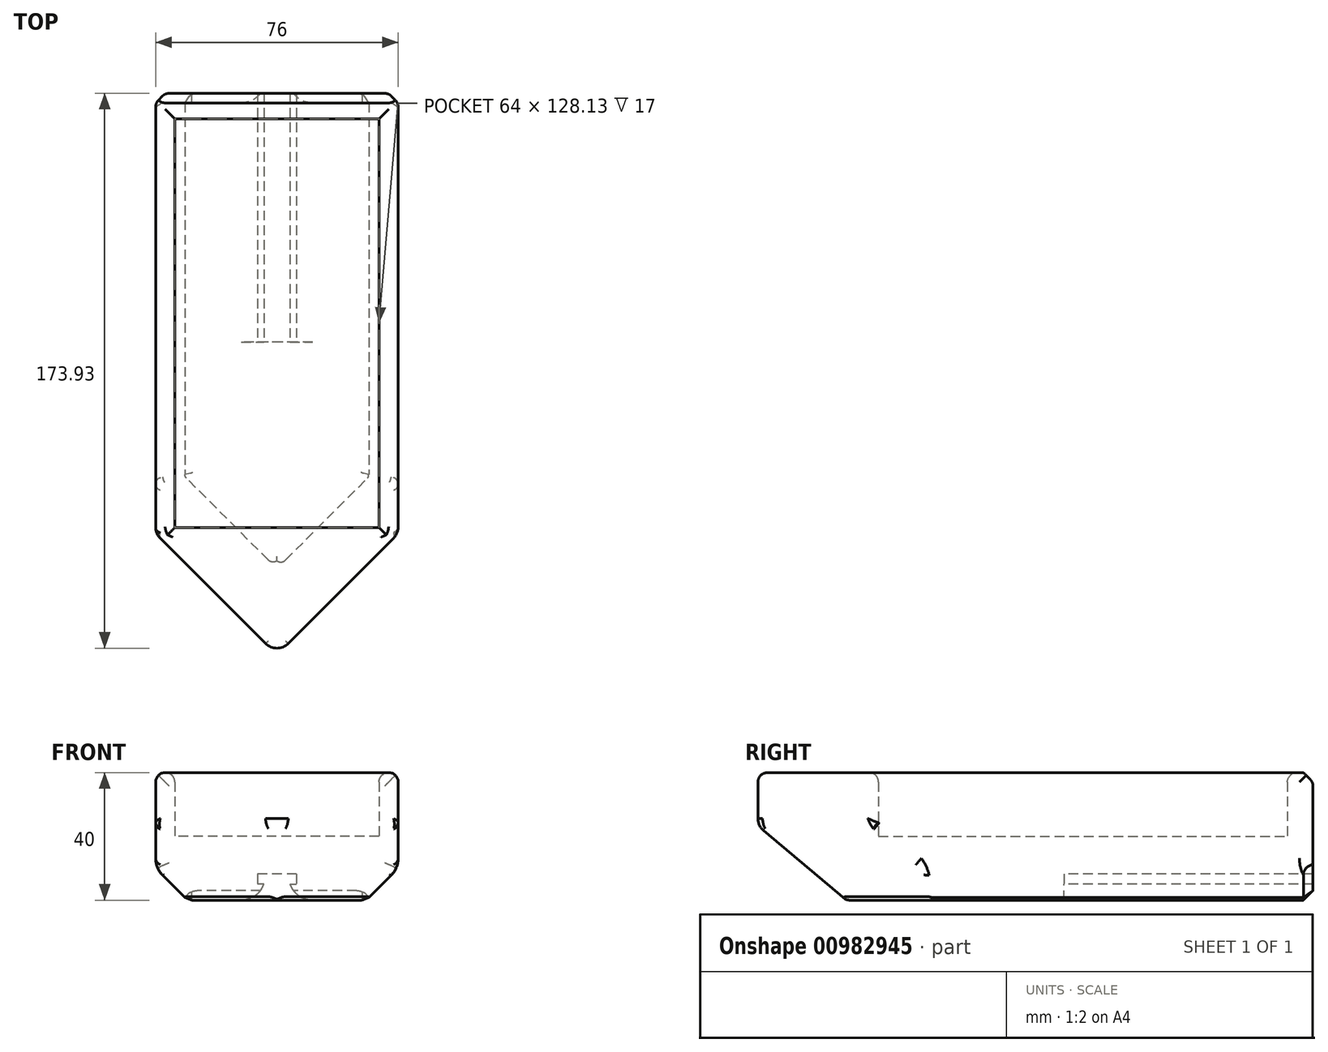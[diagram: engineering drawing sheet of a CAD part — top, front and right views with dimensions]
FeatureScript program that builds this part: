
annotation { "Feature Type Name" : "Feature", "Feature Type Description" : "" }
export const myFeature = defineFeature(function(context is Context, id is Id, definition is map)
    precondition{}
    {
        {
            var Q0;
            Q0=qCreatedBy(makeId("Front.planeOp"),FACE);
            var sketch = newSketch(context, id + "F0", { "sketchPlane" : qUnion([Q0])});
            skLineSegment(sketch, "E0", {"start": v(-6.12, 0) * mm, "end": v(-4.1, 0) * mm});
            skLineSegment(sketch, "E1", {"start": v(-4.1, 0) * mm, "end": v(-4.1, -5) * mm});
            skLineSegment(sketch, "E2", {"start": v(-4.1, -5) * mm, "end": v(-11.1, -5) * mm});
            skLineSegment(sketch, "E3", {"start": v(-11.1, -5) * mm, "end": v(-21.1, -5) * mm});
            skLineSegment(sketch, "E4", {"start": v(-6.12, 0) * mm, "end": v(-6.12, 3.2) * mm});
            skLineSegment(sketch, "E5", {"start": v(-6.12, 3.2) * mm, "end": v(0, 3.2) * mm});
            skLineSegment(sketch, "E6", {"start": v(-21.1, -5) * mm, "end": v(-38, -5) * mm});
            skLineSegment(sketch, "E7", {"start": v(-38, -5) * mm, "end": v(-38, 35) * mm});
            skLineSegment(sketch, "E8", {"start": v(-38, 35) * mm, "end": v(-32, 35) * mm});
            skLineSegment(sketch, "E9", {"start": v(-32, 35) * mm, "end": v(-32, 15) * mm});
            skLineSegment(sketch, "E10", {"start": v(-32, 15) * mm, "end": v(0, 15) * mm});
            skLineSegment(sketch, "E11", {"start": v(-32, 35) * mm, "end": v(0, 35) * mm});
            skLineSegment(sketch, "E12", {"start": v(0, 3.2) * mm, "end": v(0, 35) * mm, "construction": true});
            skLineSegment(sketch, "E13.MirrorCS", {"start": v(6.12, 0) * mm, "end": v(4.1, 0) * mm});
            skLineSegment(sketch, "E14.MirrorCS", {"start": v(6.12, 3.2) * mm, "end": v(0, 3.2) * mm});
            skLineSegment(sketch, "E15.MirrorCS", {"start": v(32, 35) * mm, "end": v(0, 35) * mm});
            skLineSegment(sketch, "E16.MirrorCS", {"start": v(6.12, 0) * mm, "end": v(6.12, 3.2) * mm});
            skLineSegment(sketch, "E17.MirrorCS", {"start": v(32, 15) * mm, "end": v(0, 15) * mm});
            skLineSegment(sketch, "E18.MirrorCS", {"start": v(11.1, -5) * mm, "end": v(21.1, -5) * mm});
            skLineSegment(sketch, "E19.MirrorCS", {"start": v(32, 35) * mm, "end": v(32, 15) * mm});
            skLineSegment(sketch, "E20.MirrorCS", {"start": v(4.1, -5) * mm, "end": v(11.1, -5) * mm});
            skLineSegment(sketch, "E21.MirrorCS", {"start": v(38, 35) * mm, "end": v(32, 35) * mm});
            skLineSegment(sketch, "E22.MirrorCS", {"start": v(4.1, 0) * mm, "end": v(4.1, -5) * mm});
            skLineSegment(sketch, "E23.MirrorCS", {"start": v(38, -5) * mm, "end": v(38, 35) * mm});
            skLineSegment(sketch, "E24.MirrorCS", {"start": v(21.1, -5) * mm, "end": v(38, -5) * mm});
            skLineSegment(sketch, "E25", {"start": v(21.1, -5) * mm, "end": v(-21.1, -5) * mm});
            skLineSegment(sketch, "E26", {"start": v(4.1, -5) * mm, "end": v(-4.1, -5) * mm});
            skSolve(sketch);
        }
        {
            var Q0;
            Q0=makeQuery(id+"F0.imprint","IMPRINT",FACE,{"disambiguationData":[TD([[makeQuery(id+"F0.imprint","IMPRINT",EDGE,{"derivedFrom":sQuery(id+"F0.wireOp",EDGE,"E0")}),-1.0]])]});
            var Q1;
            Q1=makeQuery(id+"F0.imprint","IMPRINT",FACE,{"disambiguationData":[TD([[makeQuery(id+"F0.imprint","IMPRINT",EDGE,{"derivedFrom":sQuery(id+"F0.wireOp",EDGE,"E9")}),1.0]])]});
            var Q2;
            Q2=makeQuery(id+"F0.imprint","IMPRINT",FACE,{"disambiguationData":[TD([[makeQuery(id+"F0.imprint","IMPRINT",EDGE,{"derivedFrom":sQuery(id+"F0.wireOp",EDGE,"E6")}),-1.0]])]});
            extrude(context, id + "F1", {"entities" : qUnion([Q0, Q1, Q2]), "oppositeDirection" : true, "depth" : 8 * mm, "offsetDistance" : 25 * mm});
        }
        {
            var Q0;
            Q0=makeQuery(id+"F0.imprint","IMPRINT",FACE,{"disambiguationData":[TD([[makeQuery(id+"F0.imprint","IMPRINT",EDGE,{"derivedFrom":sQuery(id+"F0.wireOp",EDGE,"E6")}),-1.0]])]});
            extrude(context, id + "F2", {"entities" : qUnion([Q0]), "operationType" : NewBodyOperationType.ADD, "depth" : 130 * mm, "offsetDistance" : 25 * mm});
        }
        {
            var Q0;
            Q0=makeQuery(id+"F0.imprint","IMPRINT",FACE,{"disambiguationData":[TD([[makeQuery(id+"F0.imprint","IMPRINT",EDGE,{"derivedFrom":sQuery(id+"F0.wireOp",EDGE,"E6")}),-1.0]])]});
            var Q1;
            Q1=makeQuery(id+"F0.imprint","IMPRINT",FACE,{"disambiguationData":[TD([[makeQuery(id+"F0.imprint","IMPRINT",EDGE,{"derivedFrom":sQuery(id+"F0.wireOp",EDGE,"E9")}),1.0]])]});
            extrude(context, id + "F3", {"entities" : qUnion([Q0, Q1]), "operationType" : NewBodyOperationType.ADD, "depth" : 170 * mm, "offsetDistance" : 25 * mm, "hasSecondDirection" : true, "secondDirectionOppositeDirection" : false, "secondDirectionDepth" : 128.13 * mm});
        }
        {
            var Q0;
            Q0=makeQuery(id+"F0.imprint","IMPRINT",FACE,{"disambiguationData":[TD([[makeQuery(id+"F0.imprint","IMPRINT",EDGE,{"derivedFrom":sQuery(id+"F0.wireOp",EDGE,"E0")}),-1.0]])]});
            extrude(context, id + "F4", {"entities" : qUnion([Q0]), "operationType" : NewBodyOperationType.ADD, "depth" : 90 * mm, "offsetDistance" : 25 * mm});
        }
        {
            var Q0;
            Q0=makeQuery(id+"F0.imprint","IMPRINT",FACE,{"disambiguationData":[TD([[makeQuery(id+"F0.imprint","IMPRINT",EDGE,{"derivedFrom":sQuery(id+"F0.wireOp",EDGE,"E0")}),-1.0]])]});
            var Q1;
            Q1=makeQuery(id+"F0.imprint","IMPRINT",FACE,{"disambiguationData":[TD([[makeQuery(id+"F0.imprint","IMPRINT",EDGE,{"derivedFrom":sQuery(id+"F0.wireOp",EDGE,"E0")}),1.0]])]});
            extrude(context, id + "F5", {"entities" : qUnion([Q0, Q1]), "operationType" : NewBodyOperationType.ADD, "depth" : 170 * mm, "offsetDistance" : 25 * mm, "hasSecondDirection" : true, "secondDirectionOppositeDirection" : false, "secondDirectionDepth" : 70 * mm});
        }
        {
            var Q0;
            Q0=makeQuery(id+"F5.opExtrude","CAP_EDGE",EDGE,{"disambiguationData":[OSD([sQuery(id+"F0.wireOp",EDGE,"E2"),sQuery(id+"F0.wireOp",EDGE,"E20.MirrorCS"),sQuery(id+"F0.wireOp",EDGE,"E26")])],"isStart":false});
            var Q1;
            {var subQ0=sQuery(id+"F0.wireOp",EDGE,"E25");var subQ1=sQuery(id+"F0.wireOp",EDGE,"E3");var subQ2=sQuery(id+"F0.wireOp",EDGE,"E6");Q1=makeQuery(id+"F12.opFillet","BLEND_EDGE",EDGE,{"blendedFrom":[makeQuery(id+"F5.boolean.opBoolean","MERGE",EDGE,{"derivedFrom":[makeQuery(id+"F4.boolean.opBoolean","MERGE",EDGE,{"derivedFrom":[makeQuery(id+"F1.opExtrude","SWEPT_EDGE",EDGE,{"disambiguationData":[OSD([subQ1,subQ2,subQ0])]}),makeQuery(id+"F4.opExtrude","SWEPT_EDGE",EDGE,{"disambiguationData":[OSD([subQ1,subQ2,subQ0])]})]}),makeQuery(id+"F5.opExtrude","SWEPT_EDGE",EDGE,{"disambiguationData":[OSD([subQ1,subQ2,subQ0])]})]}),makeQuery(id+"F5.opExtrude","CAP_FACE",FACE,{"disambiguationData":[OSD([sQuery(id+"F0.wireOp",EDGE,"E2"),subQ1,sQuery(id+"F0.wireOp",EDGE,"E18.MirrorCS"),sQuery(id+"F0.wireOp",EDGE,"E20.MirrorCS"),subQ0,sQuery(id+"F0.wireOp",EDGE,"E26")])],"isStart":false})],"blendedInto":[makeQuery(id+"F5.opExtrude","CAP_FACE",FACE,{"disambiguationData":[OSD([sQuery(id+"F0.wireOp",EDGE,"E2"),subQ1,sQuery(id+"F0.wireOp",EDGE,"E18.MirrorCS"),sQuery(id+"F0.wireOp",EDGE,"E20.MirrorCS"),subQ0,sQuery(id+"F0.wireOp",EDGE,"E26")])],"isStart":false})]});}
            chamfer(context, id + "F6", {"entities" : qUnion([Q0, Q1]), "width" : 15 * mm, "tangentPropagation" : true});
        }
        {
            var Q0;
            Q0=makeQuery(id+"F3.opExtrude","CAP_EDGE",EDGE,{"disambiguationData":[OSD([sQuery(id+"F0.wireOp",EDGE,"E23.MirrorCS")])],"isStart":false});
            var Q1;
            Q1=makeQuery(id+"F3.opExtrude","CAP_EDGE",EDGE,{"disambiguationData":[OSD([sQuery(id+"F0.wireOp",EDGE,"E7")])],"isStart":false});
            chamfer(context, id + "F7", {"entities" : qUnion([Q0, Q1]), "chamferType" : ChamferType.OFFSET_ANGLE, "width" : 40 * mm, "oppositeDirection" : false, "angle" : 45 * degree, "tangentPropagation" : true});
        }
        {
            var Q0;
            {var subQ0=sQuery(id+"F0.wireOp",EDGE,"E24.MirrorCS");var subQ1=sQuery(id+"F0.wireOp",EDGE,"E6");Q0=makeQuery(id+"F7.opChamfer","BLEND_EDGE",EDGE,{"blendedFrom":[makeQuery(id+"F3.opExtrude","CAP_EDGE",EDGE,{"disambiguationData":[OSD([sQuery(id+"F0.wireOp",EDGE,"E23.MirrorCS")])],"isStart":false}),makeQuery(id+"F3.boolean.opBoolean","MERGE",FACE,{"derivedFrom":[makeQuery(id+"F2.boolean.opBoolean","MERGE",FACE,{"derivedFrom":[makeQuery(id+"F1.opExtrude","SWEPT_FACE",FACE,{"disambiguationData":[OSD([subQ1])]}),makeQuery(id+"F2.opExtrude","SWEPT_FACE",FACE,{"disambiguationData":[OSD([subQ1])]})]}),makeQuery(id+"F2.boolean.opBoolean","MERGE",FACE,{"derivedFrom":[makeQuery(id+"F1.opExtrude","SWEPT_FACE",FACE,{"disambiguationData":[OSD([subQ0])]}),makeQuery(id+"F2.opExtrude","SWEPT_FACE",FACE,{"disambiguationData":[OSD([subQ0])]})]}),makeQuery(id+"F3.opExtrude","SWEPT_FACE",FACE,{"disambiguationData":[OSD([subQ1,subQ0,sQuery(id+"F0.wireOp",EDGE,"E25")])]})]})],"blendedInto":[makeQuery(id+"F3.boolean.opBoolean","MERGE",FACE,{"derivedFrom":[makeQuery(id+"F2.boolean.opBoolean","MERGE",FACE,{"derivedFrom":[makeQuery(id+"F1.opExtrude","SWEPT_FACE",FACE,{"disambiguationData":[OSD([subQ1])]}),makeQuery(id+"F2.opExtrude","SWEPT_FACE",FACE,{"disambiguationData":[OSD([subQ1])]})]}),makeQuery(id+"F2.boolean.opBoolean","MERGE",FACE,{"derivedFrom":[makeQuery(id+"F1.opExtrude","SWEPT_FACE",FACE,{"disambiguationData":[OSD([subQ0])]}),makeQuery(id+"F2.opExtrude","SWEPT_FACE",FACE,{"disambiguationData":[OSD([subQ0])]})]}),makeQuery(id+"F3.opExtrude","SWEPT_FACE",FACE,{"disambiguationData":[OSD([subQ1,subQ0,sQuery(id+"F0.wireOp",EDGE,"E25")])]})]})]});}
            var Q1;
            {var subQ0=sQuery(id+"F0.wireOp",EDGE,"E24.MirrorCS");var subQ1=sQuery(id+"F0.wireOp",EDGE,"E6");Q1=makeQuery(id+"F7.opChamfer","BLEND_EDGE",EDGE,{"blendedFrom":[makeQuery(id+"F3.opExtrude","CAP_EDGE",EDGE,{"disambiguationData":[OSD([sQuery(id+"F0.wireOp",EDGE,"E7")])],"isStart":false}),makeQuery(id+"F3.boolean.opBoolean","MERGE",FACE,{"derivedFrom":[makeQuery(id+"F2.boolean.opBoolean","MERGE",FACE,{"derivedFrom":[makeQuery(id+"F1.opExtrude","SWEPT_FACE",FACE,{"disambiguationData":[OSD([subQ1])]}),makeQuery(id+"F2.opExtrude","SWEPT_FACE",FACE,{"disambiguationData":[OSD([subQ1])]})]}),makeQuery(id+"F2.boolean.opBoolean","MERGE",FACE,{"derivedFrom":[makeQuery(id+"F1.opExtrude","SWEPT_FACE",FACE,{"disambiguationData":[OSD([subQ0])]}),makeQuery(id+"F2.opExtrude","SWEPT_FACE",FACE,{"disambiguationData":[OSD([subQ0])]})]}),makeQuery(id+"F3.opExtrude","SWEPT_FACE",FACE,{"disambiguationData":[OSD([subQ1,subQ0,sQuery(id+"F0.wireOp",EDGE,"E25")])]})]})],"blendedInto":[makeQuery(id+"F3.boolean.opBoolean","MERGE",FACE,{"derivedFrom":[makeQuery(id+"F2.boolean.opBoolean","MERGE",FACE,{"derivedFrom":[makeQuery(id+"F1.opExtrude","SWEPT_FACE",FACE,{"disambiguationData":[OSD([subQ1])]}),makeQuery(id+"F2.opExtrude","SWEPT_FACE",FACE,{"disambiguationData":[OSD([subQ1])]})]}),makeQuery(id+"F2.boolean.opBoolean","MERGE",FACE,{"derivedFrom":[makeQuery(id+"F1.opExtrude","SWEPT_FACE",FACE,{"disambiguationData":[OSD([subQ0])]}),makeQuery(id+"F2.opExtrude","SWEPT_FACE",FACE,{"disambiguationData":[OSD([subQ0])]})]}),makeQuery(id+"F3.opExtrude","SWEPT_FACE",FACE,{"disambiguationData":[OSD([subQ1,subQ0,sQuery(id+"F0.wireOp",EDGE,"E25")])]})]})]});}
            chamfer(context, id + "F8", {"entities" : qUnion([Q0, Q1]), "chamferType" : ChamferType.OFFSET_ANGLE, "width" : 20 * mm, "oppositeDirection" : false, "angle" : 50 * degree, "tangentPropagation" : true});
        }
        {
            var Q0;
            {var subQ0=sQuery(id+"F0.wireOp",EDGE,"E7");var subQ1=sQuery(id+"F0.wireOp",EDGE,"E6");Q0=makeQuery(id+"F3.boolean.opBoolean","MERGE",EDGE,{"derivedFrom":[makeQuery(id+"F2.boolean.opBoolean","MERGE",EDGE,{"derivedFrom":[makeQuery(id+"F1.opExtrude","SWEPT_EDGE",EDGE,{"disambiguationData":[OSD([subQ1,subQ0])]}),makeQuery(id+"F2.opExtrude","SWEPT_EDGE",EDGE,{"disambiguationData":[OSD([subQ1,subQ0])]})]}),makeQuery(id+"F3.opExtrude","SWEPT_EDGE",EDGE,{"disambiguationData":[OSD([subQ1,subQ0])]})]});}
            var Q1;
            {var subQ0=sQuery(id+"F0.wireOp",EDGE,"E24.MirrorCS");var subQ1=sQuery(id+"F0.wireOp",EDGE,"E23.MirrorCS");Q1=makeQuery(id+"F3.boolean.opBoolean","MERGE",EDGE,{"derivedFrom":[makeQuery(id+"F2.boolean.opBoolean","MERGE",EDGE,{"derivedFrom":[makeQuery(id+"F1.opExtrude","SWEPT_EDGE",EDGE,{"disambiguationData":[OSD([subQ1,subQ0])]}),makeQuery(id+"F2.opExtrude","SWEPT_EDGE",EDGE,{"disambiguationData":[OSD([subQ1,subQ0])]})]}),makeQuery(id+"F3.opExtrude","SWEPT_EDGE",EDGE,{"disambiguationData":[OSD([subQ1,subQ0])]})]});}
            chamfer(context, id + "F9", {"entities" : qUnion([Q0, Q1]), "width" : 10 * mm, "tangentPropagation" : true});
        }
        {
            var Q0;
            Q0=makeQuery(id+"F1.opExtrude","CAP_EDGE",EDGE,{"disambiguationData":[OSD([sQuery(id+"F0.wireOp",EDGE,"E8"),sQuery(id+"F0.wireOp",EDGE,"E11"),sQuery(id+"F0.wireOp",EDGE,"E15.MirrorCS"),sQuery(id+"F0.wireOp",EDGE,"E21.MirrorCS")])],"isStart":false});
            var Q1;
            Q1=makeQuery(id+"F1.opExtrude","CAP_EDGE",EDGE,{"disambiguationData":[OSD([sQuery(id+"F0.wireOp",EDGE,"E23.MirrorCS")])],"isStart":false});
            var Q2;
            {var subQ0=sQuery(id+"F0.wireOp",EDGE,"E24.MirrorCS");var subQ1=sQuery(id+"F0.wireOp",EDGE,"E23.MirrorCS");Q2=makeQuery(id+"F9.opChamfer","BLEND_EDGE",EDGE,{"blendedFrom":[makeQuery(id+"F3.boolean.opBoolean","MERGE",EDGE,{"derivedFrom":[makeQuery(id+"F2.boolean.opBoolean","MERGE",EDGE,{"derivedFrom":[makeQuery(id+"F1.opExtrude","SWEPT_EDGE",EDGE,{"disambiguationData":[OSD([subQ1,subQ0])]}),makeQuery(id+"F2.opExtrude","SWEPT_EDGE",EDGE,{"disambiguationData":[OSD([subQ1,subQ0])]})]}),makeQuery(id+"F3.opExtrude","SWEPT_EDGE",EDGE,{"disambiguationData":[OSD([subQ1,subQ0])]})]}),makeQuery(id+"F1.opExtrude","CAP_FACE",FACE,{"disambiguationData":[OSD([sQuery(id+"F0.wireOp",EDGE,"E0"),sQuery(id+"F0.wireOp",EDGE,"E1"),sQuery(id+"F0.wireOp",EDGE,"E2"),sQuery(id+"F0.wireOp",EDGE,"E3"),sQuery(id+"F0.wireOp",EDGE,"E4"),sQuery(id+"F0.wireOp",EDGE,"E5"),sQuery(id+"F0.wireOp",EDGE,"E6"),sQuery(id+"F0.wireOp",EDGE,"E7"),sQuery(id+"F0.wireOp",EDGE,"E8"),sQuery(id+"F0.wireOp",EDGE,"E11"),sQuery(id+"F0.wireOp",EDGE,"E13.MirrorCS"),sQuery(id+"F0.wireOp",EDGE,"E14.MirrorCS"),sQuery(id+"F0.wireOp",EDGE,"E15.MirrorCS"),sQuery(id+"F0.wireOp",EDGE,"E16.MirrorCS"),sQuery(id+"F0.wireOp",EDGE,"E18.MirrorCS"),sQuery(id+"F0.wireOp",EDGE,"E20.MirrorCS"),sQuery(id+"F0.wireOp",EDGE,"E21.MirrorCS"),sQuery(id+"F0.wireOp",EDGE,"E22.MirrorCS"),subQ1,subQ0])],"isStart":false})],"blendedInto":[makeQuery(id+"F1.opExtrude","CAP_FACE",FACE,{"disambiguationData":[OSD([sQuery(id+"F0.wireOp",EDGE,"E0"),sQuery(id+"F0.wireOp",EDGE,"E1"),sQuery(id+"F0.wireOp",EDGE,"E2"),sQuery(id+"F0.wireOp",EDGE,"E3"),sQuery(id+"F0.wireOp",EDGE,"E4"),sQuery(id+"F0.wireOp",EDGE,"E5"),sQuery(id+"F0.wireOp",EDGE,"E6"),sQuery(id+"F0.wireOp",EDGE,"E7"),sQuery(id+"F0.wireOp",EDGE,"E8"),sQuery(id+"F0.wireOp",EDGE,"E11"),sQuery(id+"F0.wireOp",EDGE,"E13.MirrorCS"),sQuery(id+"F0.wireOp",EDGE,"E14.MirrorCS"),sQuery(id+"F0.wireOp",EDGE,"E15.MirrorCS"),sQuery(id+"F0.wireOp",EDGE,"E16.MirrorCS"),sQuery(id+"F0.wireOp",EDGE,"E18.MirrorCS"),sQuery(id+"F0.wireOp",EDGE,"E20.MirrorCS"),sQuery(id+"F0.wireOp",EDGE,"E21.MirrorCS"),sQuery(id+"F0.wireOp",EDGE,"E22.MirrorCS"),subQ1,subQ0])],"isStart":false})]});}
            var Q3;
            Q3=makeQuery(id+"F1.opExtrude","CAP_EDGE",EDGE,{"disambiguationData":[OSD([sQuery(id+"F0.wireOp",EDGE,"E24.MirrorCS")])],"isStart":false});
            var Q4;
            Q4=makeQuery(id+"F1.opExtrude","CAP_EDGE",EDGE,{"disambiguationData":[OSD([sQuery(id+"F0.wireOp",EDGE,"E18.MirrorCS")])],"isStart":false});
            var Q5;
            Q5=makeQuery(id+"F1.opExtrude","CAP_EDGE",EDGE,{"disambiguationData":[OSD([sQuery(id+"F0.wireOp",EDGE,"E3")])],"isStart":false});
            var Q6;
            Q6=makeQuery(id+"F1.opExtrude","CAP_EDGE",EDGE,{"disambiguationData":[OSD([sQuery(id+"F0.wireOp",EDGE,"E6")])],"isStart":false});
            var Q7;
            {var subQ0=sQuery(id+"F0.wireOp",EDGE,"E7");var subQ1=sQuery(id+"F0.wireOp",EDGE,"E6");Q7=makeQuery(id+"F9.opChamfer","BLEND_EDGE",EDGE,{"blendedFrom":[makeQuery(id+"F3.boolean.opBoolean","MERGE",EDGE,{"derivedFrom":[makeQuery(id+"F2.boolean.opBoolean","MERGE",EDGE,{"derivedFrom":[makeQuery(id+"F1.opExtrude","SWEPT_EDGE",EDGE,{"disambiguationData":[OSD([subQ1,subQ0])]}),makeQuery(id+"F2.opExtrude","SWEPT_EDGE",EDGE,{"disambiguationData":[OSD([subQ1,subQ0])]})]}),makeQuery(id+"F3.opExtrude","SWEPT_EDGE",EDGE,{"disambiguationData":[OSD([subQ1,subQ0])]})]}),makeQuery(id+"F1.opExtrude","CAP_FACE",FACE,{"disambiguationData":[OSD([sQuery(id+"F0.wireOp",EDGE,"E0"),sQuery(id+"F0.wireOp",EDGE,"E1"),sQuery(id+"F0.wireOp",EDGE,"E2"),sQuery(id+"F0.wireOp",EDGE,"E3"),sQuery(id+"F0.wireOp",EDGE,"E4"),sQuery(id+"F0.wireOp",EDGE,"E5"),subQ1,subQ0,sQuery(id+"F0.wireOp",EDGE,"E8"),sQuery(id+"F0.wireOp",EDGE,"E11"),sQuery(id+"F0.wireOp",EDGE,"E13.MirrorCS"),sQuery(id+"F0.wireOp",EDGE,"E14.MirrorCS"),sQuery(id+"F0.wireOp",EDGE,"E15.MirrorCS"),sQuery(id+"F0.wireOp",EDGE,"E16.MirrorCS"),sQuery(id+"F0.wireOp",EDGE,"E18.MirrorCS"),sQuery(id+"F0.wireOp",EDGE,"E20.MirrorCS"),sQuery(id+"F0.wireOp",EDGE,"E21.MirrorCS"),sQuery(id+"F0.wireOp",EDGE,"E22.MirrorCS"),sQuery(id+"F0.wireOp",EDGE,"E23.MirrorCS"),sQuery(id+"F0.wireOp",EDGE,"E24.MirrorCS")])],"isStart":false})],"blendedInto":[makeQuery(id+"F1.opExtrude","CAP_FACE",FACE,{"disambiguationData":[OSD([sQuery(id+"F0.wireOp",EDGE,"E0"),sQuery(id+"F0.wireOp",EDGE,"E1"),sQuery(id+"F0.wireOp",EDGE,"E2"),sQuery(id+"F0.wireOp",EDGE,"E3"),sQuery(id+"F0.wireOp",EDGE,"E4"),sQuery(id+"F0.wireOp",EDGE,"E5"),subQ1,subQ0,sQuery(id+"F0.wireOp",EDGE,"E8"),sQuery(id+"F0.wireOp",EDGE,"E11"),sQuery(id+"F0.wireOp",EDGE,"E13.MirrorCS"),sQuery(id+"F0.wireOp",EDGE,"E14.MirrorCS"),sQuery(id+"F0.wireOp",EDGE,"E15.MirrorCS"),sQuery(id+"F0.wireOp",EDGE,"E16.MirrorCS"),sQuery(id+"F0.wireOp",EDGE,"E18.MirrorCS"),sQuery(id+"F0.wireOp",EDGE,"E20.MirrorCS"),sQuery(id+"F0.wireOp",EDGE,"E21.MirrorCS"),sQuery(id+"F0.wireOp",EDGE,"E22.MirrorCS"),sQuery(id+"F0.wireOp",EDGE,"E23.MirrorCS"),sQuery(id+"F0.wireOp",EDGE,"E24.MirrorCS")])],"isStart":false})]});}
            var Q8;
            Q8=makeQuery(id+"F1.opExtrude","CAP_EDGE",EDGE,{"disambiguationData":[OSD([sQuery(id+"F0.wireOp",EDGE,"E7")])],"isStart":false});
            var Q9;
            {var subQ0=sQuery(id+"F0.wireOp",EDGE,"E25");var subQ1=sQuery(id+"F0.wireOp",EDGE,"E24.MirrorCS");var subQ2=sQuery(id+"F0.wireOp",EDGE,"E6");var subQ3=sQuery(id+"F0.wireOp",EDGE,"E7");Q9=makeQuery(id+"F9.opChamfer","BLEND_EDGE",EDGE,{"blendedFrom":[makeQuery(id+"F3.boolean.opBoolean","MERGE",EDGE,{"derivedFrom":[makeQuery(id+"F2.boolean.opBoolean","MERGE",EDGE,{"derivedFrom":[makeQuery(id+"F1.opExtrude","SWEPT_EDGE",EDGE,{"disambiguationData":[OSD([subQ2,subQ3])]}),makeQuery(id+"F2.opExtrude","SWEPT_EDGE",EDGE,{"disambiguationData":[OSD([subQ2,subQ3])]})]}),makeQuery(id+"F3.opExtrude","SWEPT_EDGE",EDGE,{"disambiguationData":[OSD([subQ2,subQ3])]})]}),makeQuery(id+"F5.boolean.opBoolean","MERGE",FACE,{"derivedFrom":[makeQuery(id+"F3.boolean.opBoolean","MERGE",FACE,{"derivedFrom":[makeQuery(id+"F2.boolean.opBoolean","MERGE",FACE,{"derivedFrom":[makeQuery(id+"F1.opExtrude","SWEPT_FACE",FACE,{"disambiguationData":[OSD([subQ2,subQ0])]}),makeQuery(id+"F2.opExtrude","SWEPT_FACE",FACE,{"disambiguationData":[OSD([subQ2,subQ0])]})]}),makeQuery(id+"F3.opExtrude","SWEPT_FACE",FACE,{"disambiguationData":[OSD([subQ2,subQ0])]})]}),makeQuery(id+"F3.boolean.opBoolean","MERGE",FACE,{"derivedFrom":[makeQuery(id+"F2.boolean.opBoolean","MERGE",FACE,{"derivedFrom":[makeQuery(id+"F1.opExtrude","SWEPT_FACE",FACE,{"disambiguationData":[OSD([subQ1,subQ0])]}),makeQuery(id+"F2.opExtrude","SWEPT_FACE",FACE,{"disambiguationData":[OSD([subQ1,subQ0])]})]}),makeQuery(id+"F3.opExtrude","SWEPT_FACE",FACE,{"disambiguationData":[OSD([subQ1,subQ0])]})]}),makeQuery(id+"F5.opExtrude","SWEPT_FACE",FACE,{"disambiguationData":[OSD([subQ2,subQ1,subQ0,sQuery(id+"F0.wireOp",EDGE,"E26")])]})]})],"blendedInto":[makeQuery(id+"F5.boolean.opBoolean","MERGE",FACE,{"derivedFrom":[makeQuery(id+"F3.boolean.opBoolean","MERGE",FACE,{"derivedFrom":[makeQuery(id+"F2.boolean.opBoolean","MERGE",FACE,{"derivedFrom":[makeQuery(id+"F1.opExtrude","SWEPT_FACE",FACE,{"disambiguationData":[OSD([subQ2,subQ0])]}),makeQuery(id+"F2.opExtrude","SWEPT_FACE",FACE,{"disambiguationData":[OSD([subQ2,subQ0])]})]}),makeQuery(id+"F3.opExtrude","SWEPT_FACE",FACE,{"disambiguationData":[OSD([subQ2,subQ0])]})]}),makeQuery(id+"F3.boolean.opBoolean","MERGE",FACE,{"derivedFrom":[makeQuery(id+"F2.boolean.opBoolean","MERGE",FACE,{"derivedFrom":[makeQuery(id+"F1.opExtrude","SWEPT_FACE",FACE,{"disambiguationData":[OSD([subQ1,subQ0])]}),makeQuery(id+"F2.opExtrude","SWEPT_FACE",FACE,{"disambiguationData":[OSD([subQ1,subQ0])]})]}),makeQuery(id+"F3.opExtrude","SWEPT_FACE",FACE,{"disambiguationData":[OSD([subQ1,subQ0])]})]}),makeQuery(id+"F5.opExtrude","SWEPT_FACE",FACE,{"disambiguationData":[OSD([subQ2,subQ1,subQ0,sQuery(id+"F0.wireOp",EDGE,"E26")])]})]})]});}
            var Q10;
            {var subQ0=sQuery(id+"F0.wireOp",EDGE,"E25");var subQ1=sQuery(id+"F0.wireOp",EDGE,"E24.MirrorCS");var subQ2=sQuery(id+"F0.wireOp",EDGE,"E6");var subQ3=sQuery(id+"F0.wireOp",EDGE,"E23.MirrorCS");Q10=makeQuery(id+"F9.opChamfer","BLEND_EDGE",EDGE,{"blendedFrom":[makeQuery(id+"F3.boolean.opBoolean","MERGE",EDGE,{"derivedFrom":[makeQuery(id+"F2.boolean.opBoolean","MERGE",EDGE,{"derivedFrom":[makeQuery(id+"F1.opExtrude","SWEPT_EDGE",EDGE,{"disambiguationData":[OSD([subQ3,subQ1])]}),makeQuery(id+"F2.opExtrude","SWEPT_EDGE",EDGE,{"disambiguationData":[OSD([subQ3,subQ1])]})]}),makeQuery(id+"F3.opExtrude","SWEPT_EDGE",EDGE,{"disambiguationData":[OSD([subQ3,subQ1])]})]}),makeQuery(id+"F5.boolean.opBoolean","MERGE",FACE,{"derivedFrom":[makeQuery(id+"F3.boolean.opBoolean","MERGE",FACE,{"derivedFrom":[makeQuery(id+"F2.boolean.opBoolean","MERGE",FACE,{"derivedFrom":[makeQuery(id+"F1.opExtrude","SWEPT_FACE",FACE,{"disambiguationData":[OSD([subQ2,subQ0])]}),makeQuery(id+"F2.opExtrude","SWEPT_FACE",FACE,{"disambiguationData":[OSD([subQ2,subQ0])]})]}),makeQuery(id+"F3.opExtrude","SWEPT_FACE",FACE,{"disambiguationData":[OSD([subQ2,subQ0])]})]}),makeQuery(id+"F3.boolean.opBoolean","MERGE",FACE,{"derivedFrom":[makeQuery(id+"F2.boolean.opBoolean","MERGE",FACE,{"derivedFrom":[makeQuery(id+"F1.opExtrude","SWEPT_FACE",FACE,{"disambiguationData":[OSD([subQ1,subQ0])]}),makeQuery(id+"F2.opExtrude","SWEPT_FACE",FACE,{"disambiguationData":[OSD([subQ1,subQ0])]})]}),makeQuery(id+"F3.opExtrude","SWEPT_FACE",FACE,{"disambiguationData":[OSD([subQ1,subQ0])]})]}),makeQuery(id+"F5.opExtrude","SWEPT_FACE",FACE,{"disambiguationData":[OSD([subQ2,subQ1,subQ0,sQuery(id+"F0.wireOp",EDGE,"E26")])]})]})],"blendedInto":[makeQuery(id+"F5.boolean.opBoolean","MERGE",FACE,{"derivedFrom":[makeQuery(id+"F3.boolean.opBoolean","MERGE",FACE,{"derivedFrom":[makeQuery(id+"F2.boolean.opBoolean","MERGE",FACE,{"derivedFrom":[makeQuery(id+"F1.opExtrude","SWEPT_FACE",FACE,{"disambiguationData":[OSD([subQ2,subQ0])]}),makeQuery(id+"F2.opExtrude","SWEPT_FACE",FACE,{"disambiguationData":[OSD([subQ2,subQ0])]})]}),makeQuery(id+"F3.opExtrude","SWEPT_FACE",FACE,{"disambiguationData":[OSD([subQ2,subQ0])]})]}),makeQuery(id+"F3.boolean.opBoolean","MERGE",FACE,{"derivedFrom":[makeQuery(id+"F2.boolean.opBoolean","MERGE",FACE,{"derivedFrom":[makeQuery(id+"F1.opExtrude","SWEPT_FACE",FACE,{"disambiguationData":[OSD([subQ1,subQ0])]}),makeQuery(id+"F2.opExtrude","SWEPT_FACE",FACE,{"disambiguationData":[OSD([subQ1,subQ0])]})]}),makeQuery(id+"F3.opExtrude","SWEPT_FACE",FACE,{"disambiguationData":[OSD([subQ1,subQ0])]})]}),makeQuery(id+"F5.opExtrude","SWEPT_FACE",FACE,{"disambiguationData":[OSD([subQ2,subQ1,subQ0,sQuery(id+"F0.wireOp",EDGE,"E26")])]})]})]});}
            var Q11;
            {var subQ0=sQuery(id+"F0.wireOp",EDGE,"E25");var subQ1=sQuery(id+"F0.wireOp",EDGE,"E24.MirrorCS");var subQ2=sQuery(id+"F0.wireOp",EDGE,"E6");var subQ3=makeQuery(id+"F5.boolean.opBoolean","MERGE",FACE,{"derivedFrom":[makeQuery(id+"F3.boolean.opBoolean","MERGE",FACE,{"derivedFrom":[makeQuery(id+"F2.boolean.opBoolean","MERGE",FACE,{"derivedFrom":[makeQuery(id+"F1.opExtrude","SWEPT_FACE",FACE,{"disambiguationData":[OSD([subQ2,subQ0])]}),makeQuery(id+"F2.opExtrude","SWEPT_FACE",FACE,{"disambiguationData":[OSD([subQ2,subQ0])]})]}),makeQuery(id+"F3.opExtrude","SWEPT_FACE",FACE,{"disambiguationData":[OSD([subQ2,subQ0])]})]}),makeQuery(id+"F3.boolean.opBoolean","MERGE",FACE,{"derivedFrom":[makeQuery(id+"F2.boolean.opBoolean","MERGE",FACE,{"derivedFrom":[makeQuery(id+"F1.opExtrude","SWEPT_FACE",FACE,{"disambiguationData":[OSD([subQ1,subQ0])]}),makeQuery(id+"F2.opExtrude","SWEPT_FACE",FACE,{"disambiguationData":[OSD([subQ1,subQ0])]})]}),makeQuery(id+"F3.opExtrude","SWEPT_FACE",FACE,{"disambiguationData":[OSD([subQ1,subQ0])]})]}),makeQuery(id+"F5.opExtrude","SWEPT_FACE",FACE,{"disambiguationData":[OSD([subQ2,subQ1,subQ0,sQuery(id+"F0.wireOp",EDGE,"E26")])]})]});Q11=makeQuery(id+"F8.opChamfer","BLEND_EDGE",EDGE,{"blendedFrom":[makeQuery(id+"F7.opChamfer","BLEND_EDGE",EDGE,{"blendedFrom":[makeQuery(id+"F3.opExtrude","CAP_EDGE",EDGE,{"disambiguationData":[OSD([sQuery(id+"F0.wireOp",EDGE,"E7")])],"isStart":false}),subQ3],"blendedInto":[subQ3]}),subQ3],"blendedInto":[subQ3]});}
            var Q12;
            {var subQ0=sQuery(id+"F0.wireOp",EDGE,"E25");var subQ1=sQuery(id+"F0.wireOp",EDGE,"E24.MirrorCS");var subQ2=sQuery(id+"F0.wireOp",EDGE,"E6");var subQ3=makeQuery(id+"F5.boolean.opBoolean","MERGE",FACE,{"derivedFrom":[makeQuery(id+"F3.boolean.opBoolean","MERGE",FACE,{"derivedFrom":[makeQuery(id+"F2.boolean.opBoolean","MERGE",FACE,{"derivedFrom":[makeQuery(id+"F1.opExtrude","SWEPT_FACE",FACE,{"disambiguationData":[OSD([subQ2,subQ0])]}),makeQuery(id+"F2.opExtrude","SWEPT_FACE",FACE,{"disambiguationData":[OSD([subQ2,subQ0])]})]}),makeQuery(id+"F3.opExtrude","SWEPT_FACE",FACE,{"disambiguationData":[OSD([subQ2,subQ0])]})]}),makeQuery(id+"F3.boolean.opBoolean","MERGE",FACE,{"derivedFrom":[makeQuery(id+"F2.boolean.opBoolean","MERGE",FACE,{"derivedFrom":[makeQuery(id+"F1.opExtrude","SWEPT_FACE",FACE,{"disambiguationData":[OSD([subQ1,subQ0])]}),makeQuery(id+"F2.opExtrude","SWEPT_FACE",FACE,{"disambiguationData":[OSD([subQ1,subQ0])]})]}),makeQuery(id+"F3.opExtrude","SWEPT_FACE",FACE,{"disambiguationData":[OSD([subQ1,subQ0])]})]}),makeQuery(id+"F5.opExtrude","SWEPT_FACE",FACE,{"disambiguationData":[OSD([subQ2,subQ1,subQ0,sQuery(id+"F0.wireOp",EDGE,"E26")])]})]});Q12=makeQuery(id+"F8.opChamfer","BLEND_EDGE",EDGE,{"blendedFrom":[makeQuery(id+"F7.opChamfer","BLEND_EDGE",EDGE,{"blendedFrom":[makeQuery(id+"F3.opExtrude","CAP_EDGE",EDGE,{"disambiguationData":[OSD([sQuery(id+"F0.wireOp",EDGE,"E23.MirrorCS")])],"isStart":false}),subQ3],"blendedInto":[subQ3]}),subQ3],"blendedInto":[subQ3]});}
            chamfer(context, id + "F10", {"entities" : qUnion([Q0, Q1, Q2, Q3, Q4, Q5, Q6, Q7, Q8, Q9, Q10, Q11, Q12]), "width" : 3 * mm, "tangentPropagation" : true});
        }
        {
            var Q0;
            {var subQ0=sQuery(id+"F0.wireOp",EDGE,"E25");var subQ1=sQuery(id+"F0.wireOp",EDGE,"E24.MirrorCS");var subQ2=sQuery(id+"F0.wireOp",EDGE,"E6");var subQ3=makeQuery(id+"F5.boolean.opBoolean","MERGE",FACE,{"derivedFrom":[makeQuery(id+"F3.boolean.opBoolean","MERGE",FACE,{"derivedFrom":[makeQuery(id+"F2.boolean.opBoolean","MERGE",FACE,{"derivedFrom":[makeQuery(id+"F1.opExtrude","SWEPT_FACE",FACE,{"disambiguationData":[OSD([subQ2,subQ0])]}),makeQuery(id+"F2.opExtrude","SWEPT_FACE",FACE,{"disambiguationData":[OSD([subQ2,subQ0])]})]}),makeQuery(id+"F3.opExtrude","SWEPT_FACE",FACE,{"disambiguationData":[OSD([subQ2,subQ0])]})]}),makeQuery(id+"F3.boolean.opBoolean","MERGE",FACE,{"derivedFrom":[makeQuery(id+"F2.boolean.opBoolean","MERGE",FACE,{"derivedFrom":[makeQuery(id+"F1.opExtrude","SWEPT_FACE",FACE,{"disambiguationData":[OSD([subQ1,subQ0])]}),makeQuery(id+"F2.opExtrude","SWEPT_FACE",FACE,{"disambiguationData":[OSD([subQ1,subQ0])]})]}),makeQuery(id+"F3.opExtrude","SWEPT_FACE",FACE,{"disambiguationData":[OSD([subQ1,subQ0])]})]}),makeQuery(id+"F5.opExtrude","SWEPT_FACE",FACE,{"disambiguationData":[OSD([subQ2,subQ1,subQ0,sQuery(id+"F0.wireOp",EDGE,"E26")])]})]});var subQ4=sQuery(id+"F0.wireOp",EDGE,"E23.MirrorCS");Q0=makeQuery(id+"F10.opChamfer","BLEND_EDGE",EDGE,{"blendedFrom":[makeQuery(id+"F9.opChamfer","BLEND_EDGE",EDGE,{"blendedFrom":[makeQuery(id+"F3.boolean.opBoolean","MERGE",EDGE,{"derivedFrom":[makeQuery(id+"F2.boolean.opBoolean","MERGE",EDGE,{"derivedFrom":[makeQuery(id+"F1.opExtrude","SWEPT_EDGE",EDGE,{"disambiguationData":[OSD([subQ4,subQ1])]}),makeQuery(id+"F2.opExtrude","SWEPT_EDGE",EDGE,{"disambiguationData":[OSD([subQ4,subQ1])]})]}),makeQuery(id+"F3.opExtrude","SWEPT_EDGE",EDGE,{"disambiguationData":[OSD([subQ4,subQ1])]})]}),subQ3],"blendedInto":[subQ3]}),subQ3],"blendedInto":[subQ3]});}
            var Q1;
            {var subQ0=sQuery(id+"F0.wireOp",EDGE,"E25");var subQ1=sQuery(id+"F0.wireOp",EDGE,"E24.MirrorCS");var subQ2=sQuery(id+"F0.wireOp",EDGE,"E6");var subQ3=makeQuery(id+"F5.boolean.opBoolean","MERGE",FACE,{"derivedFrom":[makeQuery(id+"F3.boolean.opBoolean","MERGE",FACE,{"derivedFrom":[makeQuery(id+"F2.boolean.opBoolean","MERGE",FACE,{"derivedFrom":[makeQuery(id+"F1.opExtrude","SWEPT_FACE",FACE,{"disambiguationData":[OSD([subQ2,subQ0])]}),makeQuery(id+"F2.opExtrude","SWEPT_FACE",FACE,{"disambiguationData":[OSD([subQ2,subQ0])]})]}),makeQuery(id+"F3.opExtrude","SWEPT_FACE",FACE,{"disambiguationData":[OSD([subQ2,subQ0])]})]}),makeQuery(id+"F3.boolean.opBoolean","MERGE",FACE,{"derivedFrom":[makeQuery(id+"F2.boolean.opBoolean","MERGE",FACE,{"derivedFrom":[makeQuery(id+"F1.opExtrude","SWEPT_FACE",FACE,{"disambiguationData":[OSD([subQ1,subQ0])]}),makeQuery(id+"F2.opExtrude","SWEPT_FACE",FACE,{"disambiguationData":[OSD([subQ1,subQ0])]})]}),makeQuery(id+"F3.opExtrude","SWEPT_FACE",FACE,{"disambiguationData":[OSD([subQ1,subQ0])]})]}),makeQuery(id+"F5.opExtrude","SWEPT_FACE",FACE,{"disambiguationData":[OSD([subQ2,subQ1,subQ0,sQuery(id+"F0.wireOp",EDGE,"E26")])]})]});var subQ4=sQuery(id+"F0.wireOp",EDGE,"E7");Q1=makeQuery(id+"F10.opChamfer","BLEND_EDGE",EDGE,{"blendedFrom":[makeQuery(id+"F9.opChamfer","BLEND_EDGE",EDGE,{"blendedFrom":[makeQuery(id+"F3.boolean.opBoolean","MERGE",EDGE,{"derivedFrom":[makeQuery(id+"F2.boolean.opBoolean","MERGE",EDGE,{"derivedFrom":[makeQuery(id+"F1.opExtrude","SWEPT_EDGE",EDGE,{"disambiguationData":[OSD([subQ2,subQ4])]}),makeQuery(id+"F2.opExtrude","SWEPT_EDGE",EDGE,{"disambiguationData":[OSD([subQ2,subQ4])]})]}),makeQuery(id+"F3.opExtrude","SWEPT_EDGE",EDGE,{"disambiguationData":[OSD([subQ2,subQ4])]})]}),subQ3],"blendedInto":[subQ3]}),subQ3],"blendedInto":[subQ3]});}
            var Q2;
            {var subQ0=sQuery(id+"F0.wireOp",EDGE,"E25");var subQ1=sQuery(id+"F0.wireOp",EDGE,"E24.MirrorCS");var subQ2=sQuery(id+"F0.wireOp",EDGE,"E6");var subQ3=makeQuery(id+"F5.boolean.opBoolean","MERGE",FACE,{"derivedFrom":[makeQuery(id+"F3.boolean.opBoolean","MERGE",FACE,{"derivedFrom":[makeQuery(id+"F2.boolean.opBoolean","MERGE",FACE,{"derivedFrom":[makeQuery(id+"F1.opExtrude","SWEPT_FACE",FACE,{"disambiguationData":[OSD([subQ2,subQ0])]}),makeQuery(id+"F2.opExtrude","SWEPT_FACE",FACE,{"disambiguationData":[OSD([subQ2,subQ0])]})]}),makeQuery(id+"F3.opExtrude","SWEPT_FACE",FACE,{"disambiguationData":[OSD([subQ2,subQ0])]})]}),makeQuery(id+"F3.boolean.opBoolean","MERGE",FACE,{"derivedFrom":[makeQuery(id+"F2.boolean.opBoolean","MERGE",FACE,{"derivedFrom":[makeQuery(id+"F1.opExtrude","SWEPT_FACE",FACE,{"disambiguationData":[OSD([subQ1,subQ0])]}),makeQuery(id+"F2.opExtrude","SWEPT_FACE",FACE,{"disambiguationData":[OSD([subQ1,subQ0])]})]}),makeQuery(id+"F3.opExtrude","SWEPT_FACE",FACE,{"disambiguationData":[OSD([subQ1,subQ0])]})]}),makeQuery(id+"F5.opExtrude","SWEPT_FACE",FACE,{"disambiguationData":[OSD([subQ2,subQ1,subQ0,sQuery(id+"F0.wireOp",EDGE,"E26")])]})]});var subQ4=subQ3;Q2=makeQuery(id+"F10.opChamfer","BLEND_EDGE",EDGE,{"blendedFrom":[makeQuery(id+"F8.opChamfer","BLEND_EDGE",EDGE,{"blendedFrom":[makeQuery(id+"F7.opChamfer","BLEND_EDGE",EDGE,{"blendedFrom":[makeQuery(id+"F3.opExtrude","CAP_EDGE",EDGE,{"disambiguationData":[OSD([sQuery(id+"F0.wireOp",EDGE,"E23.MirrorCS")])],"isStart":false}),subQ3],"blendedInto":[subQ3]}),subQ4],"blendedInto":[subQ4]}),subQ4],"blendedInto":[subQ4]});}
            var Q3;
            {var subQ0=sQuery(id+"F0.wireOp",EDGE,"E25");var subQ1=sQuery(id+"F0.wireOp",EDGE,"E24.MirrorCS");var subQ2=sQuery(id+"F0.wireOp",EDGE,"E6");var subQ3=makeQuery(id+"F5.boolean.opBoolean","MERGE",FACE,{"derivedFrom":[makeQuery(id+"F3.boolean.opBoolean","MERGE",FACE,{"derivedFrom":[makeQuery(id+"F2.boolean.opBoolean","MERGE",FACE,{"derivedFrom":[makeQuery(id+"F1.opExtrude","SWEPT_FACE",FACE,{"disambiguationData":[OSD([subQ2,subQ0])]}),makeQuery(id+"F2.opExtrude","SWEPT_FACE",FACE,{"disambiguationData":[OSD([subQ2,subQ0])]})]}),makeQuery(id+"F3.opExtrude","SWEPT_FACE",FACE,{"disambiguationData":[OSD([subQ2,subQ0])]})]}),makeQuery(id+"F3.boolean.opBoolean","MERGE",FACE,{"derivedFrom":[makeQuery(id+"F2.boolean.opBoolean","MERGE",FACE,{"derivedFrom":[makeQuery(id+"F1.opExtrude","SWEPT_FACE",FACE,{"disambiguationData":[OSD([subQ1,subQ0])]}),makeQuery(id+"F2.opExtrude","SWEPT_FACE",FACE,{"disambiguationData":[OSD([subQ1,subQ0])]})]}),makeQuery(id+"F3.opExtrude","SWEPT_FACE",FACE,{"disambiguationData":[OSD([subQ1,subQ0])]})]}),makeQuery(id+"F5.opExtrude","SWEPT_FACE",FACE,{"disambiguationData":[OSD([subQ2,subQ1,subQ0,sQuery(id+"F0.wireOp",EDGE,"E26")])]})]});var subQ4=subQ3;Q3=makeQuery(id+"F10.opChamfer","BLEND_EDGE",EDGE,{"blendedFrom":[makeQuery(id+"F8.opChamfer","BLEND_EDGE",EDGE,{"blendedFrom":[makeQuery(id+"F7.opChamfer","BLEND_EDGE",EDGE,{"blendedFrom":[makeQuery(id+"F3.opExtrude","CAP_EDGE",EDGE,{"disambiguationData":[OSD([sQuery(id+"F0.wireOp",EDGE,"E7")])],"isStart":false}),subQ3],"blendedInto":[subQ3]}),subQ4],"blendedInto":[subQ4]}),subQ4],"blendedInto":[subQ4]});}
            fillet(context, id + "F11", {"entities" : qUnion([Q0, Q1, Q2, Q3]), "radius" : 2 * mm, "tangentPropagation" : true, "allowEdgeOverflow" : false});
        }
        {
            var Q0;
            {var subQ0=sQuery(id+"F0.wireOp",EDGE,"E7");var subQ1=sQuery(id+"F0.wireOp",EDGE,"E6");Q0=makeQuery(id+"F9.opChamfer","BLEND_EDGE",EDGE,{"blendedFrom":[makeQuery(id+"F3.boolean.opBoolean","MERGE",EDGE,{"derivedFrom":[makeQuery(id+"F2.boolean.opBoolean","MERGE",EDGE,{"derivedFrom":[makeQuery(id+"F1.opExtrude","SWEPT_EDGE",EDGE,{"disambiguationData":[OSD([subQ1,subQ0])]}),makeQuery(id+"F2.opExtrude","SWEPT_EDGE",EDGE,{"disambiguationData":[OSD([subQ1,subQ0])]})]}),makeQuery(id+"F3.opExtrude","SWEPT_EDGE",EDGE,{"disambiguationData":[OSD([subQ1,subQ0])]})]}),makeQuery(id+"F3.boolean.opBoolean","MERGE",FACE,{"derivedFrom":[makeQuery(id+"F2.boolean.opBoolean","MERGE",FACE,{"derivedFrom":[makeQuery(id+"F1.opExtrude","SWEPT_FACE",FACE,{"disambiguationData":[OSD([subQ0])]}),makeQuery(id+"F2.opExtrude","SWEPT_FACE",FACE,{"disambiguationData":[OSD([subQ0])]})]}),makeQuery(id+"F3.opExtrude","SWEPT_FACE",FACE,{"disambiguationData":[OSD([subQ0])]})]})],"blendedInto":[makeQuery(id+"F3.boolean.opBoolean","MERGE",FACE,{"derivedFrom":[makeQuery(id+"F2.boolean.opBoolean","MERGE",FACE,{"derivedFrom":[makeQuery(id+"F1.opExtrude","SWEPT_FACE",FACE,{"disambiguationData":[OSD([subQ0])]}),makeQuery(id+"F2.opExtrude","SWEPT_FACE",FACE,{"disambiguationData":[OSD([subQ0])]})]}),makeQuery(id+"F3.opExtrude","SWEPT_FACE",FACE,{"disambiguationData":[OSD([subQ0])]})]})]});}
            var Q1;
            {var subQ0=sQuery(id+"F0.wireOp",EDGE,"E25");var subQ1=sQuery(id+"F0.wireOp",EDGE,"E6");var subQ2=sQuery(id+"F0.wireOp",EDGE,"E3");Q1=makeQuery(id+"F4.boolean.opBoolean","MERGE",EDGE,{"derivedFrom":[makeQuery(id+"F1.opExtrude","SWEPT_EDGE",EDGE,{"disambiguationData":[OSD([subQ2,subQ1,subQ0])]}),makeQuery(id+"F4.opExtrude","SWEPT_EDGE",EDGE,{"disambiguationData":[OSD([subQ2,subQ1,subQ0])]})]});}
            var Q2;
            {var subQ0=sQuery(id+"F0.wireOp",EDGE,"E3");var subQ1=sQuery(id+"F0.wireOp",EDGE,"E2");Q2=makeQuery(id+"F4.boolean.opBoolean","MERGE",EDGE,{"derivedFrom":[makeQuery(id+"F1.opExtrude","SWEPT_EDGE",EDGE,{"disambiguationData":[OSD([subQ1,subQ0])]}),makeQuery(id+"F4.opExtrude","SWEPT_EDGE",EDGE,{"disambiguationData":[OSD([subQ1,subQ0])]})]});}
            var Q3;
            {var subQ0=sQuery(id+"F0.wireOp",EDGE,"E20.MirrorCS");var subQ1=sQuery(id+"F0.wireOp",EDGE,"E18.MirrorCS");Q3=makeQuery(id+"F4.boolean.opBoolean","MERGE",EDGE,{"derivedFrom":[makeQuery(id+"F1.opExtrude","SWEPT_EDGE",EDGE,{"disambiguationData":[OSD([subQ1,subQ0])]}),makeQuery(id+"F4.opExtrude","SWEPT_EDGE",EDGE,{"disambiguationData":[OSD([subQ1,subQ0])]})]});}
            var Q4;
            {var subQ0=sQuery(id+"F0.wireOp",EDGE,"E25");var subQ1=sQuery(id+"F0.wireOp",EDGE,"E24.MirrorCS");var subQ2=sQuery(id+"F0.wireOp",EDGE,"E18.MirrorCS");Q4=makeQuery(id+"F4.boolean.opBoolean","MERGE",EDGE,{"derivedFrom":[makeQuery(id+"F1.opExtrude","SWEPT_EDGE",EDGE,{"disambiguationData":[OSD([subQ2,subQ1,subQ0])]}),makeQuery(id+"F4.opExtrude","SWEPT_EDGE",EDGE,{"disambiguationData":[OSD([subQ2,subQ1,subQ0])]})]});}
            var Q5;
            {var subQ0=sQuery(id+"F0.wireOp",EDGE,"E23.MirrorCS");var subQ1=sQuery(id+"F0.wireOp",EDGE,"E24.MirrorCS");Q5=makeQuery(id+"F9.opChamfer","BLEND_EDGE",EDGE,{"blendedFrom":[makeQuery(id+"F3.boolean.opBoolean","MERGE",EDGE,{"derivedFrom":[makeQuery(id+"F2.boolean.opBoolean","MERGE",EDGE,{"derivedFrom":[makeQuery(id+"F1.opExtrude","SWEPT_EDGE",EDGE,{"disambiguationData":[OSD([subQ0,subQ1])]}),makeQuery(id+"F2.opExtrude","SWEPT_EDGE",EDGE,{"disambiguationData":[OSD([subQ0,subQ1])]})]}),makeQuery(id+"F3.opExtrude","SWEPT_EDGE",EDGE,{"disambiguationData":[OSD([subQ0,subQ1])]})]}),makeQuery(id+"F3.boolean.opBoolean","MERGE",FACE,{"derivedFrom":[makeQuery(id+"F2.boolean.opBoolean","MERGE",FACE,{"derivedFrom":[makeQuery(id+"F1.opExtrude","SWEPT_FACE",FACE,{"disambiguationData":[OSD([subQ0])]}),makeQuery(id+"F2.opExtrude","SWEPT_FACE",FACE,{"disambiguationData":[OSD([subQ0])]})]}),makeQuery(id+"F3.opExtrude","SWEPT_FACE",FACE,{"disambiguationData":[OSD([subQ0])]})]})],"blendedInto":[makeQuery(id+"F3.boolean.opBoolean","MERGE",FACE,{"derivedFrom":[makeQuery(id+"F2.boolean.opBoolean","MERGE",FACE,{"derivedFrom":[makeQuery(id+"F1.opExtrude","SWEPT_FACE",FACE,{"disambiguationData":[OSD([subQ0])]}),makeQuery(id+"F2.opExtrude","SWEPT_FACE",FACE,{"disambiguationData":[OSD([subQ0])]})]}),makeQuery(id+"F3.opExtrude","SWEPT_FACE",FACE,{"disambiguationData":[OSD([subQ0])]})]})]});}
            var Q6;
            Q6=makeQuery(id+"F6.opChamfer","BLEND_FACE",FACE,{"disambiguationData":[OSD([sQuery(id+"F0.wireOp",EDGE,"E2"),sQuery(id+"F0.wireOp",EDGE,"E20.MirrorCS"),sQuery(id+"F0.wireOp",EDGE,"E26")])]});
            fillet(context, id + "F12", {"entities" : qUnion([Q0, Q1, Q2, Q3, Q4, Q5, Q6]), "radius" : 7.5 * mm, "tangentPropagation" : true, "allowEdgeOverflow" : false});
        }
        {
            var Q0;
            {var subQ0=sQuery(id+"F0.wireOp",EDGE,"E23.MirrorCS");var subQ1=sQuery(id+"F0.wireOp",EDGE,"E25");var subQ2=sQuery(id+"F0.wireOp",EDGE,"E24.MirrorCS");var subQ3=sQuery(id+"F0.wireOp",EDGE,"E6");Q0=makeQuery(id+"F8.opChamfer","BLEND_EDGE",EDGE,{"blendedFrom":[makeQuery(id+"F7.opChamfer","BLEND_EDGE",EDGE,{"blendedFrom":[makeQuery(id+"F3.opExtrude","CAP_EDGE",EDGE,{"disambiguationData":[OSD([subQ0])],"isStart":false}),makeQuery(id+"F3.boolean.opBoolean","MERGE",FACE,{"derivedFrom":[makeQuery(id+"F2.boolean.opBoolean","MERGE",FACE,{"derivedFrom":[makeQuery(id+"F1.opExtrude","SWEPT_FACE",FACE,{"disambiguationData":[OSD([subQ3])]}),makeQuery(id+"F1.opExtrude","SWEPT_FACE",FACE,{"disambiguationData":[OSD([subQ2])]}),makeQuery(id+"F2.opExtrude","SWEPT_FACE",FACE,{"disambiguationData":[OSD([subQ3,subQ2,subQ1])]})]}),makeQuery(id+"F3.opExtrude","SWEPT_FACE",FACE,{"disambiguationData":[OSD([subQ3,subQ2,subQ1])]})]})],"blendedInto":[makeQuery(id+"F3.boolean.opBoolean","MERGE",FACE,{"derivedFrom":[makeQuery(id+"F2.boolean.opBoolean","MERGE",FACE,{"derivedFrom":[makeQuery(id+"F1.opExtrude","SWEPT_FACE",FACE,{"disambiguationData":[OSD([subQ3])]}),makeQuery(id+"F1.opExtrude","SWEPT_FACE",FACE,{"disambiguationData":[OSD([subQ2])]}),makeQuery(id+"F2.opExtrude","SWEPT_FACE",FACE,{"disambiguationData":[OSD([subQ3,subQ2,subQ1])]})]}),makeQuery(id+"F3.opExtrude","SWEPT_FACE",FACE,{"disambiguationData":[OSD([subQ3,subQ2,subQ1])]})]})]}),makeQuery(id+"F7.opChamfer","BLEND_FACE",FACE,{"disambiguationData":[OSD([subQ0])]})],"blendedInto":[makeQuery(id+"F7.opChamfer","BLEND_FACE",FACE,{"disambiguationData":[OSD([subQ0])]})]});}
            var Q1;
            {var subQ0=sQuery(id+"F0.wireOp",EDGE,"E7");var subQ1=sQuery(id+"F0.wireOp",EDGE,"E25");var subQ2=sQuery(id+"F0.wireOp",EDGE,"E24.MirrorCS");var subQ3=sQuery(id+"F0.wireOp",EDGE,"E6");Q1=makeQuery(id+"F8.opChamfer","BLEND_EDGE",EDGE,{"blendedFrom":[makeQuery(id+"F7.opChamfer","BLEND_EDGE",EDGE,{"blendedFrom":[makeQuery(id+"F3.opExtrude","CAP_EDGE",EDGE,{"disambiguationData":[OSD([subQ0])],"isStart":false}),makeQuery(id+"F3.boolean.opBoolean","MERGE",FACE,{"derivedFrom":[makeQuery(id+"F2.boolean.opBoolean","MERGE",FACE,{"derivedFrom":[makeQuery(id+"F1.opExtrude","SWEPT_FACE",FACE,{"disambiguationData":[OSD([subQ3])]}),makeQuery(id+"F1.opExtrude","SWEPT_FACE",FACE,{"disambiguationData":[OSD([subQ2])]}),makeQuery(id+"F2.opExtrude","SWEPT_FACE",FACE,{"disambiguationData":[OSD([subQ3,subQ2,subQ1])]})]}),makeQuery(id+"F3.opExtrude","SWEPT_FACE",FACE,{"disambiguationData":[OSD([subQ3,subQ2,subQ1])]})]})],"blendedInto":[makeQuery(id+"F3.boolean.opBoolean","MERGE",FACE,{"derivedFrom":[makeQuery(id+"F2.boolean.opBoolean","MERGE",FACE,{"derivedFrom":[makeQuery(id+"F1.opExtrude","SWEPT_FACE",FACE,{"disambiguationData":[OSD([subQ3])]}),makeQuery(id+"F1.opExtrude","SWEPT_FACE",FACE,{"disambiguationData":[OSD([subQ2])]}),makeQuery(id+"F2.opExtrude","SWEPT_FACE",FACE,{"disambiguationData":[OSD([subQ3,subQ2,subQ1])]})]}),makeQuery(id+"F3.opExtrude","SWEPT_FACE",FACE,{"disambiguationData":[OSD([subQ3,subQ2,subQ1])]})]})]}),makeQuery(id+"F7.opChamfer","BLEND_FACE",FACE,{"disambiguationData":[OSD([subQ0])]})],"blendedInto":[makeQuery(id+"F7.opChamfer","BLEND_FACE",FACE,{"disambiguationData":[OSD([subQ0])]})]});}
            var Q2;
            {var subQ0=sQuery(id+"F0.wireOp",EDGE,"E25");var subQ1=sQuery(id+"F0.wireOp",EDGE,"E24.MirrorCS");var subQ2=sQuery(id+"F0.wireOp",EDGE,"E6");var subQ3=makeQuery(id+"F3.boolean.opBoolean","MERGE",FACE,{"derivedFrom":[makeQuery(id+"F2.boolean.opBoolean","MERGE",FACE,{"derivedFrom":[makeQuery(id+"F1.opExtrude","SWEPT_FACE",FACE,{"disambiguationData":[OSD([subQ2])]}),makeQuery(id+"F1.opExtrude","SWEPT_FACE",FACE,{"disambiguationData":[OSD([subQ1])]}),makeQuery(id+"F2.opExtrude","SWEPT_FACE",FACE,{"disambiguationData":[OSD([subQ2,subQ1,subQ0])]})]}),makeQuery(id+"F3.opExtrude","SWEPT_FACE",FACE,{"disambiguationData":[OSD([subQ2,subQ1,subQ0])]})]});Q2=makeQuery(id+"F8.opChamfer","BLEND_EDGE",EDGE,{"blendedFrom":[makeQuery(id+"F7.opChamfer","BLEND_EDGE",EDGE,{"blendedFrom":[makeQuery(id+"F3.opExtrude","CAP_EDGE",EDGE,{"disambiguationData":[OSD([sQuery(id+"F0.wireOp",EDGE,"E7")])],"isStart":false}),subQ3],"blendedInto":[subQ3]}),makeQuery(id+"F7.opChamfer","BLEND_EDGE",EDGE,{"blendedFrom":[makeQuery(id+"F3.opExtrude","CAP_EDGE",EDGE,{"disambiguationData":[OSD([sQuery(id+"F0.wireOp",EDGE,"E23.MirrorCS")])],"isStart":false}),subQ3],"blendedInto":[subQ3]})],"blendedInto":[]});}
            var Q3;
            Q3=makeQuery(id+"F7.opChamfer","BLEND_EDGE",EDGE,{"blendedFrom":[makeQuery(id+"F3.opExtrude","CAP_EDGE",EDGE,{"disambiguationData":[OSD([sQuery(id+"F0.wireOp",EDGE,"E7")])],"isStart":false}),makeQuery(id+"F3.opExtrude","CAP_EDGE",EDGE,{"disambiguationData":[OSD([sQuery(id+"F0.wireOp",EDGE,"E23.MirrorCS")])],"isStart":false})],"blendedInto":[]});
            var Q4;
            {var subQ0=sQuery(id+"F0.wireOp",EDGE,"E23.MirrorCS");Q4=makeQuery(id+"F7.opChamfer","BLEND_EDGE",EDGE,{"blendedFrom":[makeQuery(id+"F3.opExtrude","CAP_EDGE",EDGE,{"disambiguationData":[OSD([subQ0])],"isStart":false}),makeQuery(id+"F3.boolean.opBoolean","MERGE",FACE,{"derivedFrom":[makeQuery(id+"F2.boolean.opBoolean","MERGE",FACE,{"derivedFrom":[makeQuery(id+"F1.opExtrude","SWEPT_FACE",FACE,{"disambiguationData":[OSD([subQ0])]}),makeQuery(id+"F2.opExtrude","SWEPT_FACE",FACE,{"disambiguationData":[OSD([subQ0])]})]}),makeQuery(id+"F3.opExtrude","SWEPT_FACE",FACE,{"disambiguationData":[OSD([subQ0])]})]})],"blendedInto":[makeQuery(id+"F3.boolean.opBoolean","MERGE",FACE,{"derivedFrom":[makeQuery(id+"F2.boolean.opBoolean","MERGE",FACE,{"derivedFrom":[makeQuery(id+"F1.opExtrude","SWEPT_FACE",FACE,{"disambiguationData":[OSD([subQ0])]}),makeQuery(id+"F2.opExtrude","SWEPT_FACE",FACE,{"disambiguationData":[OSD([subQ0])]})]}),makeQuery(id+"F3.opExtrude","SWEPT_FACE",FACE,{"disambiguationData":[OSD([subQ0])]})]})]});}
            var Q5;
            {var subQ0=sQuery(id+"F0.wireOp",EDGE,"E7");Q5=makeQuery(id+"F7.opChamfer","BLEND_EDGE",EDGE,{"blendedFrom":[makeQuery(id+"F3.opExtrude","CAP_EDGE",EDGE,{"disambiguationData":[OSD([subQ0])],"isStart":false}),makeQuery(id+"F3.boolean.opBoolean","MERGE",FACE,{"derivedFrom":[makeQuery(id+"F2.boolean.opBoolean","MERGE",FACE,{"derivedFrom":[makeQuery(id+"F1.opExtrude","SWEPT_FACE",FACE,{"disambiguationData":[OSD([subQ0])]}),makeQuery(id+"F2.opExtrude","SWEPT_FACE",FACE,{"disambiguationData":[OSD([subQ0])]})]}),makeQuery(id+"F3.opExtrude","SWEPT_FACE",FACE,{"disambiguationData":[OSD([subQ0])]})]})],"blendedInto":[makeQuery(id+"F3.boolean.opBoolean","MERGE",FACE,{"derivedFrom":[makeQuery(id+"F2.boolean.opBoolean","MERGE",FACE,{"derivedFrom":[makeQuery(id+"F1.opExtrude","SWEPT_FACE",FACE,{"disambiguationData":[OSD([subQ0])]}),makeQuery(id+"F2.opExtrude","SWEPT_FACE",FACE,{"disambiguationData":[OSD([subQ0])]})]}),makeQuery(id+"F3.opExtrude","SWEPT_FACE",FACE,{"disambiguationData":[OSD([subQ0])]})]})]});}
            fillet(context, id + "F13", {"entities" : qUnion([Q0, Q1, Q2, Q3, Q4, Q5]), "radius" : 5 * mm, "tangentPropagation" : true, "allowEdgeOverflow" : false});
        }
        {
            var Q0;
            Q0=makeQuery(id+"F2.opExtrude","SWEPT_EDGE",EDGE,{"disambiguationData":[OSD([sQuery(id+"F0.wireOp",EDGE,"E15.MirrorCS"),sQuery(id+"F0.wireOp",EDGE,"E19.MirrorCS"),sQuery(id+"F0.wireOp",EDGE,"E21.MirrorCS")])]});
            var Q1;
            {var subQ0=sQuery(id+"F0.wireOp",EDGE,"E23.MirrorCS");var subQ1=sQuery(id+"F0.wireOp",EDGE,"E21.MirrorCS");Q1=makeQuery(id+"F3.boolean.opBoolean","MERGE",EDGE,{"derivedFrom":[makeQuery(id+"F2.boolean.opBoolean","MERGE",EDGE,{"derivedFrom":[makeQuery(id+"F1.opExtrude","SWEPT_EDGE",EDGE,{"disambiguationData":[OSD([subQ1,subQ0])]}),makeQuery(id+"F2.opExtrude","SWEPT_EDGE",EDGE,{"disambiguationData":[OSD([subQ1,subQ0])]})]}),makeQuery(id+"F3.opExtrude","SWEPT_EDGE",EDGE,{"disambiguationData":[OSD([subQ1,subQ0])]})]});}
            var Q2;
            Q2=makeQuery(id+"F2.opExtrude","SWEPT_EDGE",EDGE,{"disambiguationData":[OSD([sQuery(id+"F0.wireOp",EDGE,"E8"),sQuery(id+"F0.wireOp",EDGE,"E9"),sQuery(id+"F0.wireOp",EDGE,"E11")])]});
            var Q3;
            {var subQ0=sQuery(id+"F0.wireOp",EDGE,"E8");var subQ1=sQuery(id+"F0.wireOp",EDGE,"E7");Q3=makeQuery(id+"F3.boolean.opBoolean","MERGE",EDGE,{"derivedFrom":[makeQuery(id+"F2.boolean.opBoolean","MERGE",EDGE,{"derivedFrom":[makeQuery(id+"F1.opExtrude","SWEPT_EDGE",EDGE,{"disambiguationData":[OSD([subQ1,subQ0])]}),makeQuery(id+"F2.opExtrude","SWEPT_EDGE",EDGE,{"disambiguationData":[OSD([subQ1,subQ0])]})]}),makeQuery(id+"F3.opExtrude","SWEPT_EDGE",EDGE,{"disambiguationData":[OSD([subQ1,subQ0])]})]});}
            var Q4;
            Q4=makeQuery(id+"F3.opExtrude","CAP_EDGE",EDGE,{"disambiguationData":[OSD([sQuery(id+"F0.wireOp",EDGE,"E8"),sQuery(id+"F0.wireOp",EDGE,"E11"),sQuery(id+"F0.wireOp",EDGE,"E15.MirrorCS"),sQuery(id+"F0.wireOp",EDGE,"E21.MirrorCS")])],"isStart":true});
            var Q5;
            {var subQ0=sQuery(id+"F0.wireOp",EDGE,"E21.MirrorCS");var subQ1=sQuery(id+"F0.wireOp",EDGE,"E15.MirrorCS");var subQ2=sQuery(id+"F0.wireOp",EDGE,"E11");var subQ3=sQuery(id+"F0.wireOp",EDGE,"E8");Q5=makeQuery(id+"F7.opChamfer","BLEND_EDGE",EDGE,{"blendedFrom":[makeQuery(id+"F3.opExtrude","CAP_EDGE",EDGE,{"disambiguationData":[OSD([sQuery(id+"F0.wireOp",EDGE,"E7")])],"isStart":false}),makeQuery(id+"F3.boolean.opBoolean","MERGE",FACE,{"derivedFrom":[makeQuery(id+"F2.boolean.opBoolean","MERGE",FACE,{"derivedFrom":[makeQuery(id+"F1.opExtrude","SWEPT_FACE",FACE,{"disambiguationData":[OSD([subQ3,subQ2,subQ1,subQ0])]}),makeQuery(id+"F2.opExtrude","SWEPT_FACE",FACE,{"disambiguationData":[OSD([subQ3])]}),makeQuery(id+"F2.opExtrude","SWEPT_FACE",FACE,{"disambiguationData":[OSD([subQ0])]})]}),makeQuery(id+"F3.opExtrude","SWEPT_FACE",FACE,{"disambiguationData":[OSD([subQ3,subQ2,subQ1,subQ0])]})]})],"blendedInto":[makeQuery(id+"F3.boolean.opBoolean","MERGE",FACE,{"derivedFrom":[makeQuery(id+"F2.boolean.opBoolean","MERGE",FACE,{"derivedFrom":[makeQuery(id+"F1.opExtrude","SWEPT_FACE",FACE,{"disambiguationData":[OSD([subQ3,subQ2,subQ1,subQ0])]}),makeQuery(id+"F2.opExtrude","SWEPT_FACE",FACE,{"disambiguationData":[OSD([subQ3])]}),makeQuery(id+"F2.opExtrude","SWEPT_FACE",FACE,{"disambiguationData":[OSD([subQ0])]})]}),makeQuery(id+"F3.opExtrude","SWEPT_FACE",FACE,{"disambiguationData":[OSD([subQ3,subQ2,subQ1,subQ0])]})]})]});}
            var Q6;
            {var subQ0=sQuery(id+"F0.wireOp",EDGE,"E21.MirrorCS");var subQ1=sQuery(id+"F0.wireOp",EDGE,"E15.MirrorCS");var subQ2=sQuery(id+"F0.wireOp",EDGE,"E11");var subQ3=sQuery(id+"F0.wireOp",EDGE,"E8");Q6=makeQuery(id+"F7.opChamfer","BLEND_EDGE",EDGE,{"blendedFrom":[makeQuery(id+"F3.opExtrude","CAP_EDGE",EDGE,{"disambiguationData":[OSD([sQuery(id+"F0.wireOp",EDGE,"E23.MirrorCS")])],"isStart":false}),makeQuery(id+"F3.boolean.opBoolean","MERGE",FACE,{"derivedFrom":[makeQuery(id+"F2.boolean.opBoolean","MERGE",FACE,{"derivedFrom":[makeQuery(id+"F1.opExtrude","SWEPT_FACE",FACE,{"disambiguationData":[OSD([subQ3,subQ2,subQ1,subQ0])]}),makeQuery(id+"F2.opExtrude","SWEPT_FACE",FACE,{"disambiguationData":[OSD([subQ3])]}),makeQuery(id+"F2.opExtrude","SWEPT_FACE",FACE,{"disambiguationData":[OSD([subQ0])]})]}),makeQuery(id+"F3.opExtrude","SWEPT_FACE",FACE,{"disambiguationData":[OSD([subQ3,subQ2,subQ1,subQ0])]})]})],"blendedInto":[makeQuery(id+"F3.boolean.opBoolean","MERGE",FACE,{"derivedFrom":[makeQuery(id+"F2.boolean.opBoolean","MERGE",FACE,{"derivedFrom":[makeQuery(id+"F1.opExtrude","SWEPT_FACE",FACE,{"disambiguationData":[OSD([subQ3,subQ2,subQ1,subQ0])]}),makeQuery(id+"F2.opExtrude","SWEPT_FACE",FACE,{"disambiguationData":[OSD([subQ3])]}),makeQuery(id+"F2.opExtrude","SWEPT_FACE",FACE,{"disambiguationData":[OSD([subQ0])]})]}),makeQuery(id+"F3.opExtrude","SWEPT_FACE",FACE,{"disambiguationData":[OSD([subQ3,subQ2,subQ1,subQ0])]})]})]});}
            var Q7;
            Q7=makeQuery(id+"F1.opExtrude","CAP_EDGE",EDGE,{"disambiguationData":[OSD([sQuery(id+"F0.wireOp",EDGE,"E8"),sQuery(id+"F0.wireOp",EDGE,"E11"),sQuery(id+"F0.wireOp",EDGE,"E15.MirrorCS"),sQuery(id+"F0.wireOp",EDGE,"E21.MirrorCS")])],"isStart":true});
            var Q8;
            {var subQ0=sQuery(id+"F0.wireOp",EDGE,"E24.MirrorCS");var subQ1=sQuery(id+"F0.wireOp",EDGE,"E23.MirrorCS");var subQ2=makeQuery(id+"F1.opExtrude","CAP_FACE",FACE,{"disambiguationData":[OSD([sQuery(id+"F0.wireOp",EDGE,"E0"),sQuery(id+"F0.wireOp",EDGE,"E1"),sQuery(id+"F0.wireOp",EDGE,"E4"),sQuery(id+"F0.wireOp",EDGE,"E5"),sQuery(id+"F0.wireOp",EDGE,"E6"),sQuery(id+"F0.wireOp",EDGE,"E7"),sQuery(id+"F0.wireOp",EDGE,"E8"),sQuery(id+"F0.wireOp",EDGE,"E11"),sQuery(id+"F0.wireOp",EDGE,"E13.MirrorCS"),sQuery(id+"F0.wireOp",EDGE,"E14.MirrorCS"),sQuery(id+"F0.wireOp",EDGE,"E15.MirrorCS"),sQuery(id+"F0.wireOp",EDGE,"E16.MirrorCS"),sQuery(id+"F0.wireOp",EDGE,"E21.MirrorCS"),sQuery(id+"F0.wireOp",EDGE,"E22.MirrorCS"),subQ1,subQ0,sQuery(id+"F0.wireOp",EDGE,"E25")])],"isStart":false});Q8=makeQuery(id+"F10.opChamfer","BLEND_EDGE",EDGE,{"blendedFrom":[makeQuery(id+"F9.opChamfer","BLEND_EDGE",EDGE,{"blendedFrom":[makeQuery(id+"F3.boolean.opBoolean","MERGE",EDGE,{"derivedFrom":[makeQuery(id+"F2.boolean.opBoolean","MERGE",EDGE,{"derivedFrom":[makeQuery(id+"F1.opExtrude","SWEPT_EDGE",EDGE,{"disambiguationData":[OSD([subQ1,subQ0])]}),makeQuery(id+"F2.opExtrude","SWEPT_EDGE",EDGE,{"disambiguationData":[OSD([subQ1,subQ0])]})]}),makeQuery(id+"F3.opExtrude","SWEPT_EDGE",EDGE,{"disambiguationData":[OSD([subQ1,subQ0])]})]}),subQ2],"blendedInto":[subQ2]}),subQ2],"blendedInto":[subQ2]});}
            var Q9;
            {var subQ0=sQuery(id+"F0.wireOp",EDGE,"E23.MirrorCS");Q9=makeQuery(id+"F10.opChamfer","BLEND_EDGE",EDGE,{"blendedFrom":[makeQuery(id+"F1.opExtrude","CAP_EDGE",EDGE,{"disambiguationData":[OSD([subQ0])],"isStart":false}),makeQuery(id+"F1.opExtrude","CAP_FACE",FACE,{"disambiguationData":[OSD([sQuery(id+"F0.wireOp",EDGE,"E0"),sQuery(id+"F0.wireOp",EDGE,"E1"),sQuery(id+"F0.wireOp",EDGE,"E4"),sQuery(id+"F0.wireOp",EDGE,"E5"),sQuery(id+"F0.wireOp",EDGE,"E6"),sQuery(id+"F0.wireOp",EDGE,"E7"),sQuery(id+"F0.wireOp",EDGE,"E8"),sQuery(id+"F0.wireOp",EDGE,"E11"),sQuery(id+"F0.wireOp",EDGE,"E13.MirrorCS"),sQuery(id+"F0.wireOp",EDGE,"E14.MirrorCS"),sQuery(id+"F0.wireOp",EDGE,"E15.MirrorCS"),sQuery(id+"F0.wireOp",EDGE,"E16.MirrorCS"),sQuery(id+"F0.wireOp",EDGE,"E21.MirrorCS"),sQuery(id+"F0.wireOp",EDGE,"E22.MirrorCS"),subQ0,sQuery(id+"F0.wireOp",EDGE,"E24.MirrorCS"),sQuery(id+"F0.wireOp",EDGE,"E25")])],"isStart":false})],"blendedInto":[makeQuery(id+"F1.opExtrude","CAP_FACE",FACE,{"disambiguationData":[OSD([sQuery(id+"F0.wireOp",EDGE,"E0"),sQuery(id+"F0.wireOp",EDGE,"E1"),sQuery(id+"F0.wireOp",EDGE,"E4"),sQuery(id+"F0.wireOp",EDGE,"E5"),sQuery(id+"F0.wireOp",EDGE,"E6"),sQuery(id+"F0.wireOp",EDGE,"E7"),sQuery(id+"F0.wireOp",EDGE,"E8"),sQuery(id+"F0.wireOp",EDGE,"E11"),sQuery(id+"F0.wireOp",EDGE,"E13.MirrorCS"),sQuery(id+"F0.wireOp",EDGE,"E14.MirrorCS"),sQuery(id+"F0.wireOp",EDGE,"E15.MirrorCS"),sQuery(id+"F0.wireOp",EDGE,"E16.MirrorCS"),sQuery(id+"F0.wireOp",EDGE,"E21.MirrorCS"),sQuery(id+"F0.wireOp",EDGE,"E22.MirrorCS"),subQ0,sQuery(id+"F0.wireOp",EDGE,"E24.MirrorCS"),sQuery(id+"F0.wireOp",EDGE,"E25")])],"isStart":false})]});}
            var Q10;
            {var subQ0=sQuery(id+"F0.wireOp",EDGE,"E7");var subQ1=sQuery(id+"F0.wireOp",EDGE,"E6");var subQ2=makeQuery(id+"F1.opExtrude","CAP_FACE",FACE,{"disambiguationData":[OSD([sQuery(id+"F0.wireOp",EDGE,"E0"),sQuery(id+"F0.wireOp",EDGE,"E1"),sQuery(id+"F0.wireOp",EDGE,"E4"),sQuery(id+"F0.wireOp",EDGE,"E5"),subQ1,subQ0,sQuery(id+"F0.wireOp",EDGE,"E8"),sQuery(id+"F0.wireOp",EDGE,"E11"),sQuery(id+"F0.wireOp",EDGE,"E13.MirrorCS"),sQuery(id+"F0.wireOp",EDGE,"E14.MirrorCS"),sQuery(id+"F0.wireOp",EDGE,"E15.MirrorCS"),sQuery(id+"F0.wireOp",EDGE,"E16.MirrorCS"),sQuery(id+"F0.wireOp",EDGE,"E21.MirrorCS"),sQuery(id+"F0.wireOp",EDGE,"E22.MirrorCS"),sQuery(id+"F0.wireOp",EDGE,"E23.MirrorCS"),sQuery(id+"F0.wireOp",EDGE,"E24.MirrorCS"),sQuery(id+"F0.wireOp",EDGE,"E25")])],"isStart":false});Q10=makeQuery(id+"F10.opChamfer","BLEND_EDGE",EDGE,{"blendedFrom":[makeQuery(id+"F9.opChamfer","BLEND_EDGE",EDGE,{"blendedFrom":[makeQuery(id+"F3.boolean.opBoolean","MERGE",EDGE,{"derivedFrom":[makeQuery(id+"F2.boolean.opBoolean","MERGE",EDGE,{"derivedFrom":[makeQuery(id+"F1.opExtrude","SWEPT_EDGE",EDGE,{"disambiguationData":[OSD([subQ1,subQ0])]}),makeQuery(id+"F2.opExtrude","SWEPT_EDGE",EDGE,{"disambiguationData":[OSD([subQ1,subQ0])]})]}),makeQuery(id+"F3.opExtrude","SWEPT_EDGE",EDGE,{"disambiguationData":[OSD([subQ1,subQ0])]})]}),subQ2],"blendedInto":[subQ2]}),subQ2],"blendedInto":[subQ2]});}
            var Q11;
            {var subQ0=sQuery(id+"F0.wireOp",EDGE,"E7");Q11=makeQuery(id+"F10.opChamfer","BLEND_EDGE",EDGE,{"blendedFrom":[makeQuery(id+"F1.opExtrude","CAP_EDGE",EDGE,{"disambiguationData":[OSD([subQ0])],"isStart":false}),makeQuery(id+"F1.opExtrude","CAP_FACE",FACE,{"disambiguationData":[OSD([sQuery(id+"F0.wireOp",EDGE,"E0"),sQuery(id+"F0.wireOp",EDGE,"E1"),sQuery(id+"F0.wireOp",EDGE,"E4"),sQuery(id+"F0.wireOp",EDGE,"E5"),sQuery(id+"F0.wireOp",EDGE,"E6"),subQ0,sQuery(id+"F0.wireOp",EDGE,"E8"),sQuery(id+"F0.wireOp",EDGE,"E11"),sQuery(id+"F0.wireOp",EDGE,"E13.MirrorCS"),sQuery(id+"F0.wireOp",EDGE,"E14.MirrorCS"),sQuery(id+"F0.wireOp",EDGE,"E15.MirrorCS"),sQuery(id+"F0.wireOp",EDGE,"E16.MirrorCS"),sQuery(id+"F0.wireOp",EDGE,"E21.MirrorCS"),sQuery(id+"F0.wireOp",EDGE,"E22.MirrorCS"),sQuery(id+"F0.wireOp",EDGE,"E23.MirrorCS"),sQuery(id+"F0.wireOp",EDGE,"E24.MirrorCS"),sQuery(id+"F0.wireOp",EDGE,"E25")])],"isStart":false})],"blendedInto":[makeQuery(id+"F1.opExtrude","CAP_FACE",FACE,{"disambiguationData":[OSD([sQuery(id+"F0.wireOp",EDGE,"E0"),sQuery(id+"F0.wireOp",EDGE,"E1"),sQuery(id+"F0.wireOp",EDGE,"E4"),sQuery(id+"F0.wireOp",EDGE,"E5"),sQuery(id+"F0.wireOp",EDGE,"E6"),subQ0,sQuery(id+"F0.wireOp",EDGE,"E8"),sQuery(id+"F0.wireOp",EDGE,"E11"),sQuery(id+"F0.wireOp",EDGE,"E13.MirrorCS"),sQuery(id+"F0.wireOp",EDGE,"E14.MirrorCS"),sQuery(id+"F0.wireOp",EDGE,"E15.MirrorCS"),sQuery(id+"F0.wireOp",EDGE,"E16.MirrorCS"),sQuery(id+"F0.wireOp",EDGE,"E21.MirrorCS"),sQuery(id+"F0.wireOp",EDGE,"E22.MirrorCS"),sQuery(id+"F0.wireOp",EDGE,"E23.MirrorCS"),sQuery(id+"F0.wireOp",EDGE,"E24.MirrorCS"),sQuery(id+"F0.wireOp",EDGE,"E25")])],"isStart":false})]});}
            var Q12;
            {var subQ0=sQuery(id+"F0.wireOp",EDGE,"E21.MirrorCS");var subQ1=sQuery(id+"F0.wireOp",EDGE,"E15.MirrorCS");var subQ2=sQuery(id+"F0.wireOp",EDGE,"E11");var subQ3=sQuery(id+"F0.wireOp",EDGE,"E8");Q12=makeQuery(id+"F10.opChamfer","BLEND_EDGE",EDGE,{"blendedFrom":[makeQuery(id+"F1.opExtrude","CAP_EDGE",EDGE,{"disambiguationData":[OSD([subQ3,subQ2,subQ1,subQ0])],"isStart":false}),makeQuery(id+"F1.opExtrude","CAP_FACE",FACE,{"disambiguationData":[OSD([sQuery(id+"F0.wireOp",EDGE,"E0"),sQuery(id+"F0.wireOp",EDGE,"E1"),sQuery(id+"F0.wireOp",EDGE,"E4"),sQuery(id+"F0.wireOp",EDGE,"E5"),sQuery(id+"F0.wireOp",EDGE,"E6"),sQuery(id+"F0.wireOp",EDGE,"E7"),subQ3,subQ2,sQuery(id+"F0.wireOp",EDGE,"E13.MirrorCS"),sQuery(id+"F0.wireOp",EDGE,"E14.MirrorCS"),subQ1,sQuery(id+"F0.wireOp",EDGE,"E16.MirrorCS"),subQ0,sQuery(id+"F0.wireOp",EDGE,"E22.MirrorCS"),sQuery(id+"F0.wireOp",EDGE,"E23.MirrorCS"),sQuery(id+"F0.wireOp",EDGE,"E24.MirrorCS"),sQuery(id+"F0.wireOp",EDGE,"E25")])],"isStart":false})],"blendedInto":[makeQuery(id+"F1.opExtrude","CAP_FACE",FACE,{"disambiguationData":[OSD([sQuery(id+"F0.wireOp",EDGE,"E0"),sQuery(id+"F0.wireOp",EDGE,"E1"),sQuery(id+"F0.wireOp",EDGE,"E4"),sQuery(id+"F0.wireOp",EDGE,"E5"),sQuery(id+"F0.wireOp",EDGE,"E6"),sQuery(id+"F0.wireOp",EDGE,"E7"),subQ3,subQ2,sQuery(id+"F0.wireOp",EDGE,"E13.MirrorCS"),sQuery(id+"F0.wireOp",EDGE,"E14.MirrorCS"),subQ1,sQuery(id+"F0.wireOp",EDGE,"E16.MirrorCS"),subQ0,sQuery(id+"F0.wireOp",EDGE,"E22.MirrorCS"),sQuery(id+"F0.wireOp",EDGE,"E23.MirrorCS"),sQuery(id+"F0.wireOp",EDGE,"E24.MirrorCS"),sQuery(id+"F0.wireOp",EDGE,"E25")])],"isStart":false})]});}
            var Q13;
            {var subQ0=sQuery(id+"F0.wireOp",EDGE,"E23.MirrorCS");Q13=makeQuery(id+"F10.opChamfer","BLEND_EDGE",EDGE,{"blendedFrom":[makeQuery(id+"F1.opExtrude","CAP_EDGE",EDGE,{"disambiguationData":[OSD([subQ0])],"isStart":false}),makeQuery(id+"F3.boolean.opBoolean","MERGE",FACE,{"derivedFrom":[makeQuery(id+"F2.boolean.opBoolean","MERGE",FACE,{"derivedFrom":[makeQuery(id+"F1.opExtrude","SWEPT_FACE",FACE,{"disambiguationData":[OSD([subQ0])]}),makeQuery(id+"F2.opExtrude","SWEPT_FACE",FACE,{"disambiguationData":[OSD([subQ0])]})]}),makeQuery(id+"F3.opExtrude","SWEPT_FACE",FACE,{"disambiguationData":[OSD([subQ0])]})]})],"blendedInto":[makeQuery(id+"F3.boolean.opBoolean","MERGE",FACE,{"derivedFrom":[makeQuery(id+"F2.boolean.opBoolean","MERGE",FACE,{"derivedFrom":[makeQuery(id+"F1.opExtrude","SWEPT_FACE",FACE,{"disambiguationData":[OSD([subQ0])]}),makeQuery(id+"F2.opExtrude","SWEPT_FACE",FACE,{"disambiguationData":[OSD([subQ0])]})]}),makeQuery(id+"F3.opExtrude","SWEPT_FACE",FACE,{"disambiguationData":[OSD([subQ0])]})]})]});}
            var Q14;
            {var subQ0=sQuery(id+"F0.wireOp",EDGE,"E7");Q14=makeQuery(id+"F10.opChamfer","BLEND_EDGE",EDGE,{"blendedFrom":[makeQuery(id+"F1.opExtrude","CAP_EDGE",EDGE,{"disambiguationData":[OSD([subQ0])],"isStart":false}),makeQuery(id+"F3.boolean.opBoolean","MERGE",FACE,{"derivedFrom":[makeQuery(id+"F2.boolean.opBoolean","MERGE",FACE,{"derivedFrom":[makeQuery(id+"F1.opExtrude","SWEPT_FACE",FACE,{"disambiguationData":[OSD([subQ0])]}),makeQuery(id+"F2.opExtrude","SWEPT_FACE",FACE,{"disambiguationData":[OSD([subQ0])]})]}),makeQuery(id+"F3.opExtrude","SWEPT_FACE",FACE,{"disambiguationData":[OSD([subQ0])]})]})],"blendedInto":[makeQuery(id+"F3.boolean.opBoolean","MERGE",FACE,{"derivedFrom":[makeQuery(id+"F2.boolean.opBoolean","MERGE",FACE,{"derivedFrom":[makeQuery(id+"F1.opExtrude","SWEPT_FACE",FACE,{"disambiguationData":[OSD([subQ0])]}),makeQuery(id+"F2.opExtrude","SWEPT_FACE",FACE,{"disambiguationData":[OSD([subQ0])]})]}),makeQuery(id+"F3.opExtrude","SWEPT_FACE",FACE,{"disambiguationData":[OSD([subQ0])]})]})]});}
            var Q15;
            {var subQ0=sQuery(id+"F0.wireOp",EDGE,"E7");var subQ1=sQuery(id+"F0.wireOp",EDGE,"E6");Q15=makeQuery(id+"F9.opChamfer","BLEND_EDGE",EDGE,{"blendedFrom":[makeQuery(id+"F3.boolean.opBoolean","MERGE",EDGE,{"derivedFrom":[makeQuery(id+"F2.boolean.opBoolean","MERGE",EDGE,{"derivedFrom":[makeQuery(id+"F1.opExtrude","SWEPT_EDGE",EDGE,{"disambiguationData":[OSD([subQ1,subQ0])]}),makeQuery(id+"F2.opExtrude","SWEPT_EDGE",EDGE,{"disambiguationData":[OSD([subQ1,subQ0])]})]}),makeQuery(id+"F3.opExtrude","SWEPT_EDGE",EDGE,{"disambiguationData":[OSD([subQ1,subQ0])]})]}),makeQuery(id+"F8.opChamfer","BLEND_FACE",FACE,{"disambiguationData":[OSD([subQ1,subQ0,sQuery(id+"F0.wireOp",EDGE,"E24.MirrorCS"),sQuery(id+"F0.wireOp",EDGE,"E25"),sQuery(id+"F0.wireOp",EDGE,"E26")])]})],"blendedInto":[makeQuery(id+"F8.opChamfer","BLEND_FACE",FACE,{"disambiguationData":[OSD([subQ1,subQ0,sQuery(id+"F0.wireOp",EDGE,"E24.MirrorCS"),sQuery(id+"F0.wireOp",EDGE,"E25"),sQuery(id+"F0.wireOp",EDGE,"E26")])]})]});}
            var Q16;
            {var subQ0=sQuery(id+"F0.wireOp",EDGE,"E24.MirrorCS");var subQ1=sQuery(id+"F0.wireOp",EDGE,"E23.MirrorCS");Q16=makeQuery(id+"F9.opChamfer","BLEND_EDGE",EDGE,{"blendedFrom":[makeQuery(id+"F3.boolean.opBoolean","MERGE",EDGE,{"derivedFrom":[makeQuery(id+"F2.boolean.opBoolean","MERGE",EDGE,{"derivedFrom":[makeQuery(id+"F1.opExtrude","SWEPT_EDGE",EDGE,{"disambiguationData":[OSD([subQ1,subQ0])]}),makeQuery(id+"F2.opExtrude","SWEPT_EDGE",EDGE,{"disambiguationData":[OSD([subQ1,subQ0])]})]}),makeQuery(id+"F3.opExtrude","SWEPT_EDGE",EDGE,{"disambiguationData":[OSD([subQ1,subQ0])]})]}),makeQuery(id+"F8.opChamfer","BLEND_FACE",FACE,{"disambiguationData":[OSD([sQuery(id+"F0.wireOp",EDGE,"E6"),subQ1,subQ0,sQuery(id+"F0.wireOp",EDGE,"E25"),sQuery(id+"F0.wireOp",EDGE,"E26")])]})],"blendedInto":[makeQuery(id+"F8.opChamfer","BLEND_FACE",FACE,{"disambiguationData":[OSD([sQuery(id+"F0.wireOp",EDGE,"E6"),subQ1,subQ0,sQuery(id+"F0.wireOp",EDGE,"E25"),sQuery(id+"F0.wireOp",EDGE,"E26")])]})]});}
            fillet(context, id + "F14", {"entities" : qUnion([Q0, Q1, Q2, Q3, Q4, Q5, Q6, Q7, Q8, Q9, Q10, Q11, Q12, Q13, Q14, Q15, Q16]), "radius" : 3 * mm, "tangentPropagation" : true, "allowEdgeOverflow" : false});
        }
    });
